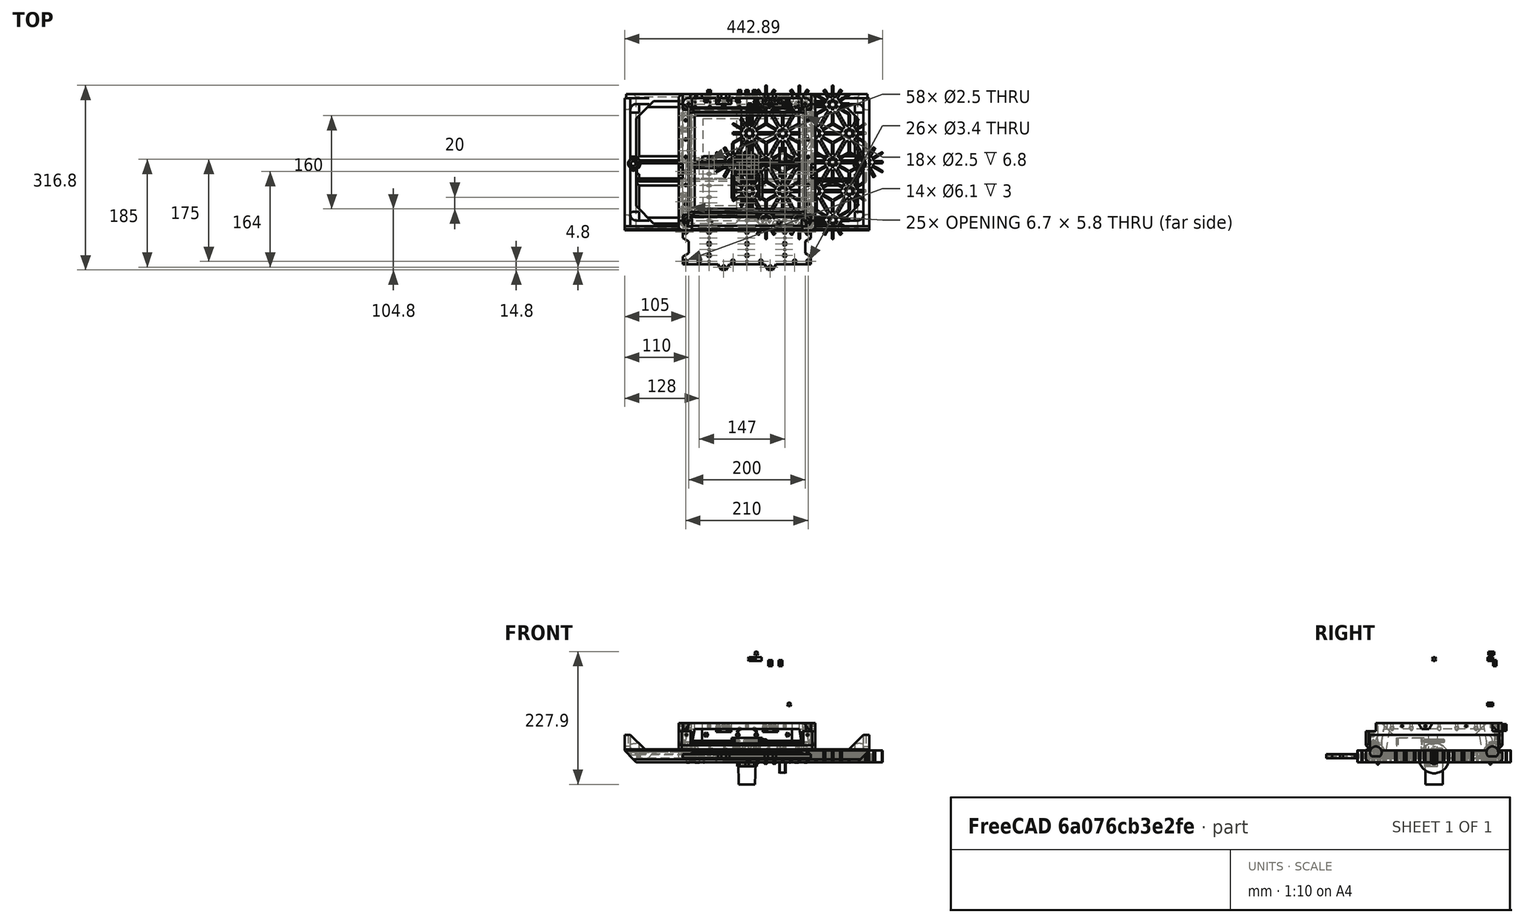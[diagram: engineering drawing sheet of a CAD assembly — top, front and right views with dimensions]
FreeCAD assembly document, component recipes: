
FREECAD ASSEMBLY — COMPONENT RECIPES ("miniXY-Frame")

This assembly document has 23 components, labeled P0..P22 below (a component is one placed body or linked part). 20 of them carry a construction recipe — the FreeCAD feature program that regenerates the part from scratch, quoted from this document or its linked companion documents; the rest are supplied as boundary geometry only. No exploded tour is included for this assembly.
NOTE — this tour is split across 3 documents so each fits a 32k-token context. This is document 1: the component sections continue in the remaining 2 documents, each repeating the header above.
COMPONENT P0 — recipe-attached ("RightPanelKumikoSakura", modeled in this document).
Construction recipe (the document's own serialized feature program — sketch geometry with constraints, then the solid features built on it; lengths are millimeters unless a unit is written):

FEATURE [Sketcher::SketchObject] Sketch076
  FullyConstrained = true
  MapMode = 5
  Support = -> [XY_Plane035]
  expr: Constraints[9] = <<Variables>>.GantorySpacing - 10
  sketch-geometry (4):
    g0: LineSegment StartX=15 StartY=95 StartZ=0 EndX=165 EndY=95 EndZ=0
    g1: LineSegment StartX=165 StartY=95 StartZ=0 EndX=165 EndY=-95 EndZ=0
    g2: LineSegment StartX=165 StartY=-95 StartZ=0 EndX=15 EndY=-95 EndZ=0
    g3: LineSegment StartX=15 StartY=-95 StartZ=0 EndX=15 EndY=95 EndZ=0
  constraints (10):
    c: Coincident(g0,g1)
    c: Coincident(g1,g2)
    c: Coincident(g2,g3)
    c: Coincident(g3,g0)
    c: Symmetric(g0,g2,g-1)
    c: Symmetric(g0,g1,g-1)
    c: DistanceX(g0) = 15
    c: Horizontal(g0)
    c: DistanceX(g0) = 165
    c: DistanceY(g1,g1) = 190
FEATURE [PartDesign::Pad] Pad021
  Direction = (0,0,1)
  Length = 7
  Length2 = 10
  Profile = -> Sketch076
  ReferenceAxis = -> Sketch076 [N_Axis]
  Reversed = true
  Type = 0
  expr: Length = <<Variables>>.WallThickness
FEATURE [PartDesign::Boolean] Boolean001
  BaseFeature = -> Pad021
  Group = -> [Clone045]
  Type = 2
FEATURE [PartDesign::Body] Body019  label="RightPanelKumikoSakura"
  Group = -> [Sketch076,Pad021,Boolean001]
  Origin = -> Origin035
  Tip = -> Boolean001
COMPONENT P1 — recipe-attached ("TopPanelInsertedNuts", modeled in this document).
Construction recipe (the document's own serialized feature program — sketch geometry with constraints, then the solid features built on it; lengths are millimeters unless a unit is written):

FEATURE [PartDesign::AdditiveBox] Box
  AttacherType = Attacher::AttachEngine3D
  AttachmentOffset = pos=(-110,-100,-1) rot=(0,0,1;0rad)
  Height = 1
  Length = 220
  MapMode = 5
  Placement = pos=(-110,-100,-1) rot=(0,0,1;0rad)
  Support = -> [XY_Plane037]
  Width = 200
  expr: .AttachmentOffset.Base.x = -(<<Variables>>.GantorySpacing + 20) / 2
  expr: .AttachmentOffset.Base.y = -<<Variables>>.GantorySpacing / 2
  expr: Length = <<Variables>>.GantorySpacing + 20
  expr: Width = <<Variables>>.GantorySpacing
FEATURE [PartDesign::AdditivePrism] Prism
  AttacherType = Attacher::AttachEngine3D
  AttachmentOffset = pos=(100,80,-1) rot=(0,0,1;0rad)
  BaseFeature = -> Box
  Circumradius = 3.35
  FirstAngle = 0
  Height = 4
  MapMode = 5
  Placement = pos=(100,80,-1) rot=(0,0,1;0rad)
  Polygon = 6
  SecondAngle = 0
  Support = -> [XY_Plane037]
  expr: .AttachmentOffset.Base.x = <<Variables>>.GantorySpacing / 2
  expr: .AttachmentOffset.Base.y = trunc((<<Variables>>.GantorySpacing - 20) / 20 / 2) * 20
FEATURE [PartDesign::AdditivePrism] Prism020
  AttacherType = Attacher::AttachEngine3D
  AttachmentOffset = pos=(-100,80,-1) rot=(0,0,1;0rad)
  BaseFeature = -> Prism
  Circumradius = 3.35
  FirstAngle = 0
  Height = 4
  MapMode = 5
  Placement = pos=(-100,80,-1) rot=(0,0,1;0rad)
  Polygon = 6
  SecondAngle = 0
  Support = -> [XY_Plane037]
  expr: .AttachmentOffset.Base.x = -<<Variables>>.GantorySpacing / 2
  expr: .AttachmentOffset.Base.y = trunc((<<Variables>>.GantorySpacing - 20) / 20 / 2) * 20
FEATURE [PartDesign::LinearPattern] LinearPattern
  BaseFeature = -> Prism020
  Direction = -> Y_Axis037
  Length = 160
  Occurrences = 9
  Originals = -> [Prism,Prism020]
  Placement = pos=(-100,80,-1) rot=(0,0,1;0rad)
  Reversed = true
  expr: Length = trunc((<<Variables>>.GantorySpacing - 1) / 20 - 1) * 20
  expr: Occurrences = trunc((<<Variables>>.GantorySpacing - 1) / 20)
FEATURE [PartDesign::Body] Body021  label="TopPanelInsertedNuts"
  Group = -> [Box,Prism,Prism020,LinearPattern]
  Origin = -> Origin037
  Tip = -> LinearPattern
COMPONENT P2 — geometry summary ("LeftPanel"; no construction recipe available for this part):
  bounding box: 234.0 x 210.0 x 47.0 mm
  tessellated surface: 684 triangles
  volume: 478904856520590275852955231166615715246145621785509215956463249338484086506495282965888048924409776630849818438009607219283139737538738958728098922627072 mm^3 (20735582076420394415876391785394331561649271033872828819312797242641532115541347280385334868308949145231766654478375564196134222345893274777731203072% of its bounding box)
COMPONENT P3 — geometry summary ("LeftPullyMount"; no construction recipe available for this part):
  bounding box: 24.0 x 23.0 x 23.0 mm
  tessellated surface: 248 triangles
  volume: 299315535325368910778677430749424573239660087407870710314527759839463589562716364963451420763389337175224325103538955539851616635702864912651435768807424 mm^3 (2360107169195797858979530859132323100612416590760435877303002830261131174156394113953131164970302059916367937818172666815640445996735709350483468484608% of its bounding box)
COMPONENT P4 — recipe-attached ("PullyIdler", modeled in this document).
Construction recipe (the document's own serialized feature program — sketch geometry with constraints, then the solid features built on it; lengths are millimeters unless a unit is written):

FEATURE [Sketcher::SketchObject] Sketch004
  FullyConstrained = true
  MapMode = 5
  Placement = pos=(0,0,0) rot=(1,0,0;1.5708rad)
  Support = -> [XZ_Plane003]
  expr: Constraints[19] = <<Variables>>.PullyDiameterIdler / 2
  sketch-geometry (8):
    g0: LineSegment StartX=2.5 StartY=4.25 StartZ=0 EndX=2.5 EndY=-4.25 EndZ=0
    g1: LineSegment StartX=2.5 StartY=-4.25 StartZ=0 EndX=9 EndY=-4.25 EndZ=0
    g2: LineSegment StartX=9 StartY=-4.25 StartZ=0 EndX=9 EndY=-3.25 EndZ=0
    g3: LineSegment StartX=9 StartY=-3.25 StartZ=0 EndX=6.365 EndY=-3.25 EndZ=0
    g4: LineSegment StartX=6.365 StartY=-3.25 StartZ=0 EndX=6.365 EndY=3.25 EndZ=0
    g5: LineSegment StartX=6.365 StartY=3.25 StartZ=0 EndX=9 EndY=3.25 EndZ=0
    g6: LineSegment StartX=9 StartY=3.25 StartZ=0 EndX=9 EndY=4.25 EndZ=0
    g7: LineSegment StartX=9 StartY=4.25 StartZ=0 EndX=2.5 EndY=4.25 EndZ=0
  constraints (22):
    c: Coincident(g0,g1)
    c: Horizontal(g1)
    c: Coincident(g1,g2)
    c: Vertical(g2)
    c: Coincident(g2,g3)
    c: Horizontal(g3)
    c: Coincident(g3,g4)
    c: Coincident(g4,g5)
    c: Horizontal(g5)
    c: Coincident(g5,g6)
    c: Vertical(g6)
    c: Coincident(g6,g7)
    c: Coincident(g7,g0)
    c: Horizontal(g7)
    c: Symmetric(g0,g0,g-1)
    c: Symmetric(g4,g3,g-1)
    c: DistanceY(g6,g6) = 1
    c: DistanceY(g4,g4) = 6.5
    c: DistanceX(g-1,g0) = 2.5
    c: DistanceX(g-1,g4) = 6.365
    c: DistanceX(g-1,g6) = 9
    c: Vertical(g2,g5)
FEATURE [PartDesign::Revolution] Revolution
  Angle = 360
  Axis = (0,-2e-16,1)
  Base = (0,0,0)
  Placement = pos=(0,0,0) rot=(1,0,0;1.5708rad)
  Profile = -> Sketch004
  ReferenceAxis = -> Sketch004 [V_Axis]
FEATURE [PartDesign::Body] Body  label="IdlerBody"
  Group = -> [Sketch004,Revolution]
  Origin = -> Origin003
  Tip = -> Revolution
COMPONENT P5 — recipe-attached ("CarriageLeft", modeled in this document).
Construction recipe (the document's own serialized feature program — sketch geometry with constraints, then the solid features built on it; lengths are millimeters unless a unit is written):

FEATURE [Sketcher::SketchObject] Sketch
  FullyConstrained = true
  MapMode = 5
  Support = -> [XY_Plane006]
  sketch-geometry (19):
    g0: LineSegment StartX=-7.5 StartY=16 StartZ=0 EndX=7.5 EndY=16 EndZ=0
    g1: LineSegment StartX=7.5 StartY=-16 StartZ=0 EndX=-7.5 EndY=-16 EndZ=0
    g2: LineSegment StartX=-10 StartY=-13.5 StartZ=0 EndX=-10 EndY=13.5 EndZ=0
    g3: LineSegment StartX=20.7665 StartY=5 StartZ=0 EndX=48 EndY=5 EndZ=0
    g4: LineSegment StartX=50 StartY=3 StartZ=0 EndX=50 EndY=-3 EndZ=0
    g5: LineSegment StartX=48 StartY=-5 StartZ=0 EndX=20.7665 EndY=-5 EndZ=0
    g6: ArcOfCircle CenterX=20.7665 CenterY=-16 CenterZ=0 NormalX=0 NormalY=0 NormalZ=1 AngleXU=0 Radius=11 StartAngle=1.5708 EndAngle=2.95533
    g7: ArcOfCircle CenterX=20.7665 CenterY=16 CenterZ=0 NormalX=0 NormalY=0 NormalZ=1 AngleXU=0 Radius=11 StartAngle=3.32785 EndAngle=4.71239
    g8: ArcOfCircle CenterX=-7.5 CenterY=13.5 CenterZ=0 NormalX=0 NormalY=0 NormalZ=1 AngleXU=0 Radius=2.5 StartAngle=1.5708 EndAngle=3.14159
    g9: GeomPoint X=-10 Y=16 Z=0
    g10: ArcOfCircle CenterX=-7.5 CenterY=-13.5 CenterZ=0 NormalX=0 NormalY=0 NormalZ=1 AngleXU=0 Radius=2.5 StartAngle=3.14159 EndAngle=4.71239
    g11: GeomPoint X=-10 Y=-16 Z=0
    g12: ArcOfCircle CenterX=7.5 CenterY=-13.5 CenterZ=0 NormalX=0 NormalY=0 NormalZ=1 AngleXU=0 Radius=2.5 StartAngle=4.71239 EndAngle=6.09693
    g13: ArcOfCircle CenterX=7.5 CenterY=13.5 CenterZ=0 NormalX=0 NormalY=0 NormalZ=1 AngleXU=0 Radius=2.5 StartAngle=0.18626 EndAngle=1.5708
    g14: GeomPoint X=10 Y=16 Z=0
    g15: ArcOfCircle CenterX=48 CenterY=3 CenterZ=0 NormalX=0 NormalY=0 NormalZ=1 AngleXU=0 Radius=2 StartAngle=-9e-16 EndAngle=1.5708
    g16: GeomPoint X=50 Y=5 Z=0
    g17: ArcOfCircle CenterX=48 CenterY=-3 CenterZ=0 NormalX=0 NormalY=0 NormalZ=1 AngleXU=0 Radius=2 StartAngle=4.71239 EndAngle=6.28319
    g18: GeomPoint X=50 Y=-5 Z=0
  constraints (40):
    c: Horizontal(g3)
    c: Symmetric(g9,g11,g-1)
    c: Symmetric(g16,g18,g-1)
    c: DistanceY(g11,g9) = 32
    c: Symmetric(g9,g14,g-2)
    c: DistanceY(g18,g16) = 10
    c: DistanceX(g-1,g16) = 50
    c: Symmetric(g7,g6,g-1)
    c: PointOnObject(g9,g0)
    c: PointOnObject(g9,g2)
    c: Tangent(g0,g8) = 1.5708
    c: Tangent(g2,g8) = 1.5708
    c: PointOnObject(g11,g2)
    c: PointOnObject(g11,g1)
    c: Tangent(g2,g10) = 1.5708
    c: Tangent(g1,g10) = 1.5708
    c: Tangent(g1,g12) = 1.5708
    c: PointOnObject(g14,g0)
    c: Tangent(g0,g13) = 1.5708
    c: Equal(g8,g10)
    c: Equal(g8,g12)
    c: Radius(g8) = 2.5
    c: DistanceX(g9,g14) = 20
    c: Tangent(g13,g7) = 1.5708
    c: Tangent(g12,g6) = 1.5708
    c: PointOnObject(g7,g0)
    c: Symmetric(g8,g13,g-2)
    c: Symmetric(g12,g13,g-1)
    c: Tangent(g7,g3) = -1.5708
    c: Tangent(g6,g5) = -1.5708
    c: PointOnObject(g16,g3)
    c: PointOnObject(g16,g4)
    c: Tangent(g3,g15) = 1.5708
    c: Tangent(g4,g15) = 1.5708
    c: PointOnObject(g18,g5)
    c: PointOnObject(g18,g4)
    c: Tangent(g5,g17) = 1.5708
    c: Tangent(g4,g17) = 1.5708
    c: Equal(g15,g17)
    c: Radius(g15) = 2
FEATURE [PartDesign::Pad] Pad
  Direction = (0,0,1)
  Length = 7
  Length2 = 10
  Profile = -> Sketch
  ReferenceAxis = -> Sketch [N_Axis]
  Type = 0
FEATURE [Sketcher::SketchObject] Sketch005
  AttachmentOffset = pos=(0,0,10) rot=(0,0,1;0rad)
  FullyConstrained = true
  MapMode = 5
  Placement = pos=(0,0,10) rot=(0,0,1;0rad)
  Support = -> [XY_Plane006]
  sketch-geometry (4):
    g0: Circle CenterX=-7.5 CenterY=5 CenterZ=0 NormalX=0 NormalY=0 NormalZ=1 AngleXU=0 Radius=1.5
    g1: Circle CenterX=-7.5 CenterY=-5 CenterZ=0 NormalX=0 NormalY=0 NormalZ=1 AngleXU=0 Radius=1.5
    g2: Circle CenterX=7.5 CenterY=-5 CenterZ=0 NormalX=0 NormalY=0 NormalZ=1 AngleXU=0 Radius=1.5
    g3: Circle CenterX=7.5 CenterY=5 CenterZ=0 NormalX=0 NormalY=0 NormalZ=1 AngleXU=0 Radius=1.5
  constraints (9):
    c: Symmetric(g0,g1,g-1)
    c: Symmetric(g3,g2,g-1)
    c: Symmetric(g0,g3,g-2)
    c: DistanceX(g0,g3) = 15
    c: DistanceY(g1,g0) = 10
    c: Equal(g0,g1)
    c: Equal(g0,g2)
    c: Equal(g0,g3)
    c: Diameter(g0) = 3
FEATURE [Sketcher::SketchObject] Sketch006
  FullyConstrained = true
  MapMode = 5
  Support = -> [XY_Plane006]
  sketch-geometry (2):
    g0: Circle CenterX=0 CenterY=0 CenterZ=0 NormalX=0 NormalY=0 NormalZ=1 AngleXU=0 Radius=1.5
    g1: Circle CenterX=12.73 CenterY=0 CenterZ=0 NormalX=0 NormalY=0 NormalZ=1 AngleXU=0 Radius=1.5
  constraints (5):
    c: Coincident(g0,g-1)
    c: PointOnObject(g1,g-1)
    c: Equal(g0,g1)
    c: Diameter(g0) = 3
    c: DistanceX(g0,g1) = 12.73
FEATURE [PartDesign::Chamfer] Chamfer
  Angle = 45
  Base = -> Pad [Face16]
  BaseFeature = -> Pad
  ChamferType = 0
  FlipDirection = false
  Size = 1
  Size2 = 1
  SupportTransform = false
  UseAllEdges = false
FEATURE [Sketcher::SketchObject] Sketch007
  FullyConstrained = true
  MapMode = 5
  Support = -> [XY_Plane006]
  sketch-geometry (2):
    g0: Circle CenterX=20 CenterY=0 CenterZ=0 NormalX=0 NormalY=0 NormalZ=1 AngleXU=0 Radius=1.5
    g1: Circle CenterX=40 CenterY=0 CenterZ=0 NormalX=0 NormalY=0 NormalZ=1 AngleXU=0 Radius=1.5
  constraints (6):
    c: PointOnObject(g0,g-1)
    c: PointOnObject(g1,g-1)
    c: DistanceX(g-1,g0) = 20
    c: DistanceX(g0,g1) = 20
    c: Equal(g0,g1)
    c: Diameter(g0) = 3
FEATURE [Sketcher::SketchObject] Sketch008
  AttachmentOffset = pos=(0,0,16.5) rot=(0,0,1;0rad)
  FullyConstrained = true
  MapMode = 5
  Placement = pos=(0,0,16.5) rot=(0,0,1;0rad)
  Support = -> [XY_Plane006]
  sketch-geometry (6):
    g0: LineSegment StartX=9.5 StartY=5 StartZ=0 EndX=26 EndY=5 EndZ=0
    g1: LineSegment StartX=24 StartY=3 StartZ=0 EndX=24 EndY=-3 EndZ=0
    g2: LineSegment StartX=26 StartY=-5 StartZ=0 EndX=9.5 EndY=-5 EndZ=0
    g3: LineSegment StartX=9.5 StartY=-5 StartZ=0 EndX=9.5 EndY=5 EndZ=0
    g4: ArcOfCircle CenterX=26 CenterY=3 CenterZ=0 NormalX=0 NormalY=0 NormalZ=1 AngleXU=0 Radius=2 StartAngle=1.5708 EndAngle=3.14159
    g5: ArcOfCircle CenterX=26 CenterY=-3 CenterZ=0 NormalX=0 NormalY=0 NormalZ=1 AngleXU=0 Radius=2 StartAngle=3.14159 EndAngle=4.71239
  constraints (14):
    c: Horizontal(g0)
    c: Coincident(g0,g3)
    c: Symmetric(g2,g0,g-1)
    c: Coincident(g3,g2)
    c: Tangent(g4,g1) = -1.5708
    c: Tangent(g4,g0) = 1.5708
    c: Tangent(g5,g1) = -1.5708
    c: Tangent(g5,g2) = 1.5708
    c: Symmetric(g4,g5,g-1)
    c: Equal(g4,g5)
    c: Radius(g4) = 2
    c: DistanceY(g3,g3) = 10
    c: DistanceX(g0,g1) = 14.5
    c: DistanceX(g-1,g0) = 9.5
FEATURE [Sketcher::SketchObject] Sketch009
  FullyConstrained = true
  MapMode = 5
  Support = -> [XY_Plane006]
  sketch-geometry (36):
    g0: LineSegment StartX=11.5 StartY=5 StartZ=0 EndX=30 EndY=5 EndZ=0
    g1: LineSegment StartX=32 StartY=3 StartZ=0 EndX=32 EndY=-3 EndZ=0
    g2: LineSegment StartX=30 StartY=-5 StartZ=0 EndX=11.5 EndY=-5 EndZ=0
    g3: LineSegment StartX=9.5 StartY=-3 StartZ=0 EndX=9.5 EndY=3 EndZ=0
    g4: LineSegment StartX=-3 StartY=16 StartZ=0 EndX=3 EndY=16 EndZ=0
    g5: LineSegment StartX=5 StartY=14 StartZ=0 EndX=5 EndY=12 EndZ=0
    g6: LineSegment StartX=3 StartY=10 StartZ=0 EndX=-3 EndY=10 EndZ=0
    g7: LineSegment StartX=-5 StartY=12 StartZ=0 EndX=-5 EndY=14 EndZ=0
    g8: LineSegment StartX=-3 StartY=-10 StartZ=0 EndX=3 EndY=-10 EndZ=0
    g9: LineSegment StartX=5 StartY=-12 StartZ=0 EndX=5 EndY=-14 EndZ=0
    g10: LineSegment StartX=3 StartY=-16 StartZ=0 EndX=-3 EndY=-16 EndZ=0
    g11: LineSegment StartX=-5 StartY=-14 StartZ=0 EndX=-5 EndY=-12 EndZ=0
    g12: ArcOfCircle CenterX=-3 CenterY=14 CenterZ=0 NormalX=0 NormalY=0 NormalZ=1 AngleXU=0 Radius=2 StartAngle=1.5708 EndAngle=3.14159
    g13: GeomPoint X=-5 Y=16 Z=0
    g14: ArcOfCircle CenterX=-3 CenterY=12 CenterZ=0 NormalX=0 NormalY=0 NormalZ=1 AngleXU=0 Radius=2 StartAngle=3.14159 EndAngle=4.71239
    g15: GeomPoint X=-5 Y=10 Z=0
    g16: ArcOfCircle CenterX=3 CenterY=12 CenterZ=0 NormalX=0 NormalY=0 NormalZ=1 AngleXU=0 Radius=2 StartAngle=4.71239 EndAngle=6.28319
    g17: GeomPoint X=5 Y=10 Z=0
    g18: ArcOfCircle CenterX=3 CenterY=14 CenterZ=0 NormalX=0 NormalY=0 NormalZ=1 AngleXU=0 Radius=2 StartAngle=1e-16 EndAngle=1.5708
    g19: GeomPoint X=5 Y=16 Z=0
    g20: ArcOfCircle CenterX=-3 CenterY=-12 CenterZ=0 NormalX=0 NormalY=0 NormalZ=1 AngleXU=0 Radius=2 StartAngle=1.5708 EndAngle=3.14159
    g21: GeomPoint X=-5 Y=-10 Z=0
    g22: ArcOfCircle CenterX=-3 CenterY=-14 CenterZ=0 NormalX=0 NormalY=0 NormalZ=1 AngleXU=0 Radius=2 StartAngle=3.14159 EndAngle=4.71239
    g23: GeomPoint X=-5 Y=-16 Z=0
    g24: ArcOfCircle CenterX=3 CenterY=-14 CenterZ=0 NormalX=0 NormalY=0 NormalZ=1 AngleXU=0 Radius=2 StartAngle=4.71239 EndAngle=6.28319
    g25: GeomPoint X=5 Y=-16 Z=0
    g26: ArcOfCircle CenterX=3 CenterY=-12 CenterZ=0 NormalX=0 NormalY=0 NormalZ=1 AngleXU=0 Radius=2 StartAngle=0 EndAngle=1.5708
    g27: GeomPoint X=5 Y=-10 Z=0
    g28: ArcOfCircle CenterX=11.5 CenterY=3 CenterZ=0 NormalX=0 NormalY=0 NormalZ=1 AngleXU=0 Radius=2 StartAngle=1.5708 EndAngle=3.14159
    g29: GeomPoint X=9.5 Y=5 Z=0
    g30: ArcOfCircle CenterX=11.5 CenterY=-3 CenterZ=0 NormalX=0 NormalY=0 NormalZ=1 AngleXU=0 Radius=2 StartAngle=3.14159 EndAngle=4.71239
    g31: GeomPoint X=9.5 Y=-5 Z=0
    g32: ArcOfCircle CenterX=30 CenterY=-3 CenterZ=0 NormalX=0 NormalY=0 NormalZ=1 AngleXU=0 Radius=2 StartAngle=4.71239 EndAngle=6.28319
    g33: GeomPoint X=32 Y=-5 Z=0
    g34: ArcOfCircle CenterX=30 CenterY=3 CenterZ=0 NormalX=0 NormalY=0 NormalZ=1 AngleXU=0 Radius=2 StartAngle=3e-16 EndAngle=1.5708
    g35: GeomPoint X=32 Y=5 Z=0
  constraints (76):
    c: Horizontal(g0)
    c: Symmetric(g29,g31,g-1)
    c: Symmetric(g35,g33,g-1)
    c: DistanceY(g31,g29) = 10
    c: DistanceX(g29,g35) = 22.5
    c: Vertical(g7)
    c: Symmetric(g13,g19,g-2)
    c: Symmetric(g15,g17,g-2)
    c: Symmetric(g21,g15,g-1)
    c: Symmetric(g13,g23,g-1)
    c: Symmetric(g17,g27,g-1)
    c: Symmetric(g19,g25,g-1)
    c: DistanceY(g23,g13) = 32
    c: DistanceX(g13,g19) = 10
    c: DistanceY(g15,g13) = 6
    c: DistanceX(g-1,g35) = 32
    c: PointOnObject(g13,g4)
    c: PointOnObject(g13,g7)
    c: Tangent(g4,g12) = 1.5708
    c: Tangent(g7,g12) = 1.5708
    c: PointOnObject(g15,g7)
    c: PointOnObject(g15,g6)
    c: Tangent(g7,g14) = 1.5708
    c: Tangent(g6,g14) = 1.5708
    c: PointOnObject(g17,g6)
    c: PointOnObject(g17,g5)
    c: Tangent(g6,g16) = 1.5708
    c: Tangent(g5,g16) = 1.5708
    c: PointOnObject(g19,g5)
    c: PointOnObject(g19,g4)
    c: Tangent(g5,g18) = 1.5708
    c: Tangent(g4,g18) = 1.5708
    c: PointOnObject(g21,g8)
    c: PointOnObject(g21,g11)
    c: Tangent(g8,g20) = 1.5708
    c: Tangent(g11,g20) = 1.5708
    c: PointOnObject(g23,g11)
    c: PointOnObject(g23,g10)
    c: Tangent(g11,g22) = 1.5708
    c: Tangent(g10,g22) = 1.5708
    c: PointOnObject(g25,g10)
    c: PointOnObject(g25,g9)
    c: Tangent(g10,g24) = 1.5708
    c: Tangent(g9,g24) = 1.5708
    c: PointOnObject(g27,g9)
    c: PointOnObject(g27,g8)
    c: Tangent(g9,g26) = 1.5708
    c: Tangent(g8,g26) = 1.5708
    c: PointOnObject(g29,g0)
    c: PointOnObject(g29,g3)
    c: Tangent(g0,g28) = 1.5708
    c: Tangent(g3,g28) = 1.5708
    c: PointOnObject(g31,g3)
    c: PointOnObject(g31,g2)
    c: Tangent(g3,g30) = 1.5708
    c: Tangent(g2,g30) = 1.5708
    c: PointOnObject(g33,g2)
    c: PointOnObject(g33,g1)
    c: Tangent(g2,g32) = 1.5708
    c: Tangent(g1,g32) = 1.5708
    c: PointOnObject(g35,g1)
    c: PointOnObject(g35,g0)
    c: Tangent(g1,g34) = 1.5708
    c: Tangent(g0,g34) = 1.5708
    c: Equal(g12,g14)
    c: Equal(g12,g16)
    c: Equal(g12,g18)
    c: Equal(g12,g20)
    c: Equal(g12,g22)
    c: Equal(g12,g24)
    c: Equal(g12,g26)
    c: Equal(g12,g28)
    c: Equal(g12,g30)
    c: Equal(g12,g32)
    c: Equal(g12,g34)
    c: Radius(g12) = 2
FEATURE [Sketcher::SketchObject] Sketch010
  FullyConstrained = true
  MapMode = 5
  Support = -> [XY_Plane006]
  sketch-geometry (2):
    g0: Circle CenterX=0 CenterY=13 CenterZ=0 NormalX=0 NormalY=0 NormalZ=1 AngleXU=0 Radius=1.5
    g1: Circle CenterX=0 CenterY=-13 CenterZ=0 NormalX=0 NormalY=0 NormalZ=1 AngleXU=0 Radius=1.5
  constraints (5):
    c: PointOnObject(g0,g-2)
    c: Symmetric(g0,g1,g-1)
    c: DistanceY(g1,g0) = 26
    c: Equal(g0,g1)
    c: Diameter(g0) = 3
FEATURE [Sketcher::SketchObject] Sketch011
  AttachmentOffset = pos=(0,0,27) rot=(0,0,1;0rad)
  FullyConstrained = true
  MapMode = 5
  Placement = pos=(0,0,27) rot=(0,0,1;0rad)
  Support = -> [XY_Plane008]
  sketch-geometry (8):
    g0: LineSegment StartX=-5 StartY=18 StartZ=0 EndX=5 EndY=18 EndZ=0
    g1: LineSegment StartX=5 StartY=-18 StartZ=0 EndX=-5 EndY=-18 EndZ=0
    g2: LineSegment StartX=-5 StartY=-18 StartZ=0 EndX=-5 EndY=18 EndZ=0
    g3: LineSegment StartX=18.5 StartY=4.5 StartZ=0 EndX=34 EndY=4.5 EndZ=0
    g4: LineSegment StartX=34 StartY=4.5 StartZ=0 EndX=34 EndY=-4.5 EndZ=0
    g5: LineSegment StartX=34 StartY=-4.5 StartZ=0 EndX=18.5 EndY=-4.5 EndZ=0
    g6: ArcOfCircle CenterX=18.5 CenterY=-18 CenterZ=0 NormalX=0 NormalY=0 NormalZ=1 AngleXU=0 Radius=13.5 StartAngle=1.5708 EndAngle=3.14159
    g7: ArcOfCircle CenterX=18.5 CenterY=18 CenterZ=0 NormalX=0 NormalY=0 NormalZ=1 AngleXU=0 Radius=13.5 StartAngle=3.14159 EndAngle=4.71239
  constraints (21):
    c: Coincident(g1,g2)
    c: Coincident(g2,g0)
    c: Coincident(g3,g4)
    c: Coincident(g4,g5)
    c: Horizontal(g3)
    c: Symmetric(g0,g1,g-1)
    c: Symmetric(g3,g5,g-1)
    c: Symmetric(g3,g4,g-1)
    c: DistanceY(g2,g2) = 36
    c: DistanceX(g0,g0) = 10
    c: Symmetric(g0,g0,g-2)
    c: DistanceY(g4,g4) = 9
    c: Symmetric(g0,g1,g-1)
    c: DistanceX(g-1,g3) = 34
    c: Coincident(g6,g5)
    c: Coincident(g6,g1)
    c: Coincident(g7,g0)
    c: Coincident(g7,g3)
    c: Symmetric(g7,g6,g-1)
    c: Vertical(g7,g3)
    c: Horizontal(g0,g7)
FEATURE [PartDesign::Pad] Pad003
  Direction = (0,0,1)
  Length = 5
  Length2 = 10
  Profile = -> Sketch011
  ReferenceAxis = -> Sketch011 [N_Axis]
  Type = 0
FEATURE [PartDesign::SubtractiveBox] Box003
  AttacherType = Attacher::AttachEngine3D
  AttachmentOffset = pos=(-3.1,9.9,0) rot=(0,0,1;0rad)
  BaseFeature = -> Pad003
  Height = 28
  Length = 6.2
  MapMode = 5
  Placement = pos=(-3.1,9.9,0) rot=(0,0,1;0rad)
  Support = -> [XY_Plane008]
  Width = 6.2
FEATURE [PartDesign::SubtractiveBox] Box004
  AttacherType = Attacher::AttachEngine3D
  AttachmentOffset = pos=(-3.1,-16.1,0) rot=(0,0,1;0rad)
  BaseFeature = -> Box003
  Height = 28
  Length = 6.2
  MapMode = 5
  Placement = pos=(-3.1,-16.1,0) rot=(0,0,1;0rad)
  Support = -> [XY_Plane008]
  Width = 6.2
FEATURE [PartDesign::SubtractiveBox] Box005
  AttacherType = Attacher::AttachEngine3D
  AttachmentOffset = pos=(23.9,-3.1,0) rot=(0,0,1;0rad)
  BaseFeature = -> Box004
  Height = 28
  Length = 8.2
  MapMode = 5
  Placement = pos=(23.9,-3.1,0) rot=(0,0,1;0rad)
  Support = -> [XY_Plane008]
  Width = 6.2
FEATURE [PartDesign::Fillet] Fillet002
  Base = -> Box005 [Edge41,Edge57,Edge49,Edge39,Edge55,Edge47,Edge45,Edge37,Edge53,Edge59,Edge51,Edge43]
  BaseFeature = -> Box005
  Placement = pos=(23.9,-3.1,0) rot=(0,0,1;0rad)
  Radius = 0.8
  SupportTransform = false
  UseAllEdges = false
FEATURE [PartDesign::Fillet] Fillet003
  Base = -> Fillet002 [Edge56,Edge52,Edge62,Edge50,Edge49,Edge58]
  BaseFeature = -> Fillet002
  Placement = pos=(23.9,-3.1,0) rot=(0,0,1;0rad)
  Radius = 2.5
  SupportTransform = false
  UseAllEdges = false
FEATURE [PartDesign::Chamfer] Chamfer001
  Angle = 45
  Base = -> Fillet003 [Edge4]
  BaseFeature = -> Fillet003
  ChamferType = 0
  FlipDirection = false
  Placement = pos=(23.9,-3.1,0) rot=(0,0,1;0rad)
  Size = 1
  Size2 = 1
  SupportTransform = false
  UseAllEdges = false
FEATURE [PartDesign::Chamfer] Chamfer002
  Angle = 45
  Base = -> Chamfer001 [Edge116]
  BaseFeature = -> Chamfer001
  ChamferType = 0
  FlipDirection = false
  Placement = pos=(23.9,-3.1,0) rot=(0,0,1;0rad)
  Size = 1
  Size2 = 1
  SupportTransform = false
  UseAllEdges = false
FEATURE [Sketcher::SketchObject] Sketch012
  AttachmentOffset = pos=(0,0,32) rot=(0,0,1;0rad)
  FullyConstrained = true
  MapMode = 5
  Placement = pos=(0,0,32) rot=(0,0,1;0rad)
  Support = -> [XY_Plane008]
  expr: Constraints[4] = <<Variables>>.PullyDiameterIdler
  sketch-geometry (2):
    g0: Circle CenterX=0 CenterY=0 CenterZ=0 NormalX=0 NormalY=0 NormalZ=1 AngleXU=0 Radius=1.5
    g1: Circle CenterX=12.73 CenterY=0 CenterZ=0 NormalX=0 NormalY=0 NormalZ=1 AngleXU=0 Radius=1.5
  constraints (5):
    c: Coincident(g0,g-1)
    c: PointOnObject(g1,g-1)
    c: Equal(g0,g1)
    c: Diameter(g0) = 3
    c: DistanceX(g0,g1) = 12.73
FEATURE [PartDesign::Hole] Hole004
  BaseFeature = -> Chamfer002
  CustomThreadClearance = 0
  Depth = 98.3182
  DepthType = 1
  Diameter = 5.5
  DrillForDepth = false
  DrillPoint = 1
  DrillPointAngle = 118
  HoleCutCountersinkAngle = 90
  HoleCutCustomValues = false
  HoleCutDepth = 5.4
  HoleCutDiameter = 10.1
  HoleCutType = 0
  ModelThread = false
  Placement = pos=(23.9,-3.1,0) rot=(0,0,1;0rad)
  Profile = -> Sketch012
  Tapered = false
  TaperedAngle = 90
  ThreadClass = 0
  ThreadDepth = 98.3182
  ThreadDepthType = 0
  ThreadDirection = 0
  ThreadFit = 0
  ThreadSize = 13
  ThreadType = 1
  Threaded = false
  UseCustomThreadClearance = false
FEATURE [Sketcher::SketchObject] Sketch013
  AttachmentOffset = pos=(0,0,32) rot=(0,0,1;0rad)
  FullyConstrained = true
  MapMode = 5
  Placement = pos=(0,0,32) rot=(0,0,1;0rad)
  Support = -> [XY_Plane008]
  sketch-geometry (3):
    g0: Circle CenterX=0 CenterY=13 CenterZ=0 NormalX=0 NormalY=0 NormalZ=1 AngleXU=0 Radius=1.5
    g1: Circle CenterX=0 CenterY=-13 CenterZ=0 NormalX=0 NormalY=0 NormalZ=1 AngleXU=0 Radius=1.5
    g2: Circle CenterX=28 CenterY=0 CenterZ=0 NormalX=0 NormalY=0 NormalZ=1 AngleXU=0 Radius=1.5
  constraints (8):
    c: PointOnObject(g0,g-2)
    c: PointOnObject(g2,g-1)
    c: Symmetric(g0,g1,g-1)
    c: DistanceY(g1,g0) = 26
    c: DistanceX(g-1,g2) = 28
    c: Equal(g0,g1)
    c: Equal(g0,g2)
    c: Diameter(g0) = 3
FEATURE [PartDesign::Hole] Hole005
  BaseFeature = -> Hole004
  CustomThreadClearance = 0
  Depth = 98.3182
  DepthType = 1
  Diameter = 3.4
  DrillForDepth = false
  DrillPoint = 1
  DrillPointAngle = 118
  HoleCutCountersinkAngle = 90
  HoleCutCustomValues = false
  HoleCutDepth = 1.7
  HoleCutDiameter = 6
  HoleCutType = 9
  ModelThread = false
  Placement = pos=(23.9,-3.1,0) rot=(0,0,1;0rad)
  Profile = -> Sketch013
  Tapered = false
  TaperedAngle = 90
  ThreadClass = 0
  ThreadDepth = 98.3182
  ThreadDepthType = 0
  ThreadDirection = 0
  ThreadFit = 0
  ThreadSize = 9
  ThreadType = 1
  Threaded = false
  UseCustomThreadClearance = false
FEATURE [Sketcher::SketchObject] Sketch078
  FullyConstrained = true
  MapMode = 5
  Support = -> [XY_Plane006]
  sketch-geometry (24):
    g0: LineSegment StartX=-3 StartY=16 StartZ=0 EndX=3 EndY=16 EndZ=0
    g1: LineSegment StartX=5 StartY=14 StartZ=0 EndX=5 EndY=12 EndZ=0
    g2: LineSegment StartX=3 StartY=10 StartZ=0 EndX=-3 EndY=10 EndZ=0
    g3: LineSegment StartX=-5 StartY=12 StartZ=0 EndX=-5 EndY=14 EndZ=0
    g4: LineSegment StartX=-3 StartY=-10 StartZ=0 EndX=3 EndY=-10 EndZ=0
    g5: LineSegment StartX=5 StartY=-12 StartZ=0 EndX=5 EndY=-14 EndZ=0
    g6: LineSegment StartX=3 StartY=-16 StartZ=0 EndX=-3 EndY=-16 EndZ=0
    g7: LineSegment StartX=-5 StartY=-14 StartZ=0 EndX=-5 EndY=-12 EndZ=0
    g8: ArcOfCircle CenterX=-3 CenterY=14 CenterZ=0 NormalX=0 NormalY=0 NormalZ=1 AngleXU=0 Radius=2 StartAngle=1.5708 EndAngle=3.14159
    g9: GeomPoint X=-5 Y=16 Z=0
    g10: ArcOfCircle CenterX=-3 CenterY=12 CenterZ=0 NormalX=0 NormalY=0 NormalZ=1 AngleXU=0 Radius=2 StartAngle=3.14159 EndAngle=4.71239
    g11: GeomPoint X=-5 Y=10 Z=0
    g12: ArcOfCircle CenterX=3 CenterY=12 CenterZ=0 NormalX=0 NormalY=0 NormalZ=1 AngleXU=0 Radius=2 StartAngle=4.71239 EndAngle=6.28319
    g13: GeomPoint X=5 Y=10 Z=0
    g14: ArcOfCircle CenterX=3 CenterY=14 CenterZ=0 NormalX=0 NormalY=0 NormalZ=1 AngleXU=0 Radius=2 StartAngle=0 EndAngle=1.5708
    g15: GeomPoint X=5 Y=16 Z=0
    g16: ArcOfCircle CenterX=-3 CenterY=-12 CenterZ=0 NormalX=0 NormalY=0 NormalZ=1 AngleXU=0 Radius=2 StartAngle=1.5708 EndAngle=3.14159
    g17: GeomPoint X=-5 Y=-10 Z=0
    g18: ArcOfCircle CenterX=-3 CenterY=-14 CenterZ=0 NormalX=0 NormalY=0 NormalZ=1 AngleXU=0 Radius=2 StartAngle=3.14159 EndAngle=4.71239
    g19: GeomPoint X=-5 Y=-16 Z=0
    g20: ArcOfCircle CenterX=3 CenterY=-14 CenterZ=0 NormalX=0 NormalY=0 NormalZ=1 AngleXU=0 Radius=2 StartAngle=4.71239 EndAngle=6.28319
    g21: GeomPoint X=5 Y=-16 Z=0
    g22: ArcOfCircle CenterX=3 CenterY=-12 CenterZ=0 NormalX=0 NormalY=0 NormalZ=1 AngleXU=0 Radius=2 StartAngle=0 EndAngle=1.5708
    g23: GeomPoint X=5 Y=-10 Z=0
  constraints (50):
    c: Vertical(g3)
    c: Symmetric(g9,g15,g-2)
    c: Symmetric(g11,g13,g-2)
    c: Symmetric(g17,g11,g-1)
    c: Symmetric(g9,g19,g-1)
    c: Symmetric(g13,g23,g-1)
    c: Symmetric(g15,g21,g-1)
    c: DistanceY(g19,g9) = 32
    c: DistanceX(g9,g15) = 10
    c: DistanceY(g11,g9) = 6
    c: PointOnObject(g9,g0)
    c: PointOnObject(g9,g3)
    c: Tangent(g0,g8) = 1.5708
    c: Tangent(g3,g8) = 1.5708
    c: PointOnObject(g11,g3)
    c: PointOnObject(g11,g2)
    c: Tangent(g3,g10) = 1.5708
    c: Tangent(g2,g10) = 1.5708
    c: PointOnObject(g13,g2)
    c: PointOnObject(g13,g1)
    c: Tangent(g2,g12) = 1.5708
    c: Tangent(g1,g12) = 1.5708
    c: PointOnObject(g15,g1)
    c: PointOnObject(g15,g0)
    c: Tangent(g1,g14) = 1.5708
    c: Tangent(g0,g14) = 1.5708
    c: PointOnObject(g17,g4)
    c: PointOnObject(g17,g7)
    c: Tangent(g4,g16) = 1.5708
    c: Tangent(g7,g16) = 1.5708
    c: PointOnObject(g19,g7)
    c: PointOnObject(g19,g6)
    c: Tangent(g7,g18) = 1.5708
    c: Tangent(g6,g18) = 1.5708
    c: PointOnObject(g21,g6)
    c: PointOnObject(g21,g5)
    c: Tangent(g6,g20) = 1.5708
    c: Tangent(g5,g20) = 1.5708
    c: PointOnObject(g23,g5)
    c: PointOnObject(g23,g4)
    c: Tangent(g5,g22) = 1.5708
    c: Tangent(g4,g22) = 1.5708
    c: Equal(g8,g10)
    c: Equal(g8,g12)
    c: Equal(g8,g14)
    c: Equal(g8,g16)
    c: Equal(g8,g18)
    c: Equal(g8,g20)
    c: Equal(g8,g22)
    c: Radius(g8) = 2
FEATURE [Sketcher::SketchObject] Sketch079
  FullyConstrained = true
  MapMode = 5
  Support = -> [XY_Plane006]
  sketch-geometry (12):
    g0: LineSegment StartX=11.5 StartY=5 StartZ=0 EndX=14 EndY=5 EndZ=0
    g1: LineSegment StartX=16 StartY=3 StartZ=0 EndX=16 EndY=-3 EndZ=0
    g2: LineSegment StartX=14 StartY=-5 StartZ=0 EndX=11.5 EndY=-5 EndZ=0
    g3: LineSegment StartX=9.5 StartY=-3 StartZ=0 EndX=9.5 EndY=3 EndZ=0
    g4: ArcOfCircle CenterX=11.5 CenterY=3 CenterZ=0 NormalX=0 NormalY=0 NormalZ=1 AngleXU=0 Radius=2 StartAngle=1.5708 EndAngle=3.14159
    g5: GeomPoint X=9.5 Y=5 Z=0
    g6: ArcOfCircle CenterX=11.5 CenterY=-3 CenterZ=0 NormalX=0 NormalY=0 NormalZ=1 AngleXU=0 Radius=2 StartAngle=3.14159 EndAngle=4.71239
    g7: GeomPoint X=9.5 Y=-5 Z=0
    g8: ArcOfCircle CenterX=14 CenterY=-3 CenterZ=0 NormalX=0 NormalY=0 NormalZ=1 AngleXU=0 Radius=2 StartAngle=4.71239 EndAngle=6.28319
    g9: GeomPoint X=16 Y=-5 Z=0
    g10: ArcOfCircle CenterX=14 CenterY=3 CenterZ=0 NormalX=0 NormalY=0 NormalZ=1 AngleXU=0 Radius=2 StartAngle=0 EndAngle=1.5708
    g11: GeomPoint X=16 Y=5 Z=0
  constraints (26):
    c: Horizontal(g0)
    c: Symmetric(g5,g7,g-1)
    c: Symmetric(g11,g9,g-1)
    c: DistanceY(g7,g5) = 10
    c: DistanceX(g5,g11) = 6.5
    c: PointOnObject(g5,g0)
    c: PointOnObject(g5,g3)
    c: Tangent(g0,g4) = 1.5708
    c: Tangent(g3,g4) = 1.5708
    c: PointOnObject(g7,g3)
    c: PointOnObject(g7,g2)
    c: Tangent(g3,g6) = 1.5708
    c: Tangent(g2,g6) = 1.5708
    c: PointOnObject(g9,g2)
    c: PointOnObject(g9,g1)
    c: Tangent(g2,g8) = 1.5708
    c: Tangent(g1,g8) = 1.5708
    c: PointOnObject(g11,g1)
    c: PointOnObject(g11,g0)
    c: Tangent(g1,g10) = 1.5708
    c: Tangent(g0,g10) = 1.5708
    c: DistanceX(g-1,g5) = 9.5
    c: Equal(g4,g10)
    c: Equal(g4,g6)
    c: Equal(g4,g8)
    c: Radius(g4) = 2
FEATURE [PartDesign::Pad] Pad023
  BaseFeature = -> Chamfer
  Direction = (0,0,1)
  Length = 16.5
  Length2 = 10
  Profile = -> Sketch079
  ReferenceAxis = -> Sketch079 [N_Axis]
  Type = 0
FEATURE [Sketcher::SketchObject] Sketch080
  FullyConstrained = true
  MapMode = 5
  Placement = pos=(0,0,0) rot=(0.57735,0.57735,0.57735;2.0944rad)
  Support = -> [YZ_Plane006]
  sketch-geometry (15):
    g0: LineSegment StartX=-17 StartY=26 StartZ=0 EndX=-15 EndY=28 EndZ=0
    g1: LineSegment StartX=-11 StartY=28 StartZ=0 EndX=-9 EndY=26 EndZ=0
    g2: LineSegment StartX=-9 StartY=26 StartZ=0 EndX=-7 EndY=26 EndZ=0
    g3: LineSegment StartX=-7 StartY=26 StartZ=0 EndX=-5 EndY=28 EndZ=0
    g4: LineSegment StartX=-5 StartY=28 StartZ=0 EndX=5 EndY=28 EndZ=0
    g5: LineSegment StartX=5 StartY=28 StartZ=0 EndX=7 EndY=26 EndZ=0
    g6: LineSegment StartX=7 StartY=26 StartZ=0 EndX=9 EndY=26 EndZ=0
    g7: LineSegment StartX=9 StartY=26 StartZ=0 EndX=11 EndY=28 EndZ=0
    g8: LineSegment StartX=11 StartY=28 StartZ=0 EndX=15 EndY=28 EndZ=0
    g9: LineSegment StartX=15 StartY=28 StartZ=0 EndX=17 EndY=26 EndZ=0
    g10: LineSegment StartX=17 StartY=26 StartZ=0 EndX=17 EndY=32 EndZ=0
    g11: LineSegment StartX=17 StartY=32 StartZ=0 EndX=-17 EndY=32 EndZ=0
    g12: LineSegment StartX=-17 StartY=32 StartZ=0 EndX=-17 EndY=26 EndZ=0
    g13: LineSegment StartX=-15 StartY=28 StartZ=0 EndX=-13 EndY=28 EndZ=0
    g14: LineSegment StartX=-13 StartY=28 StartZ=0 EndX=-11 EndY=28 EndZ=0
  constraints (37):
    c: Coincident(g0,g13)
    c: Coincident(g14,g1)
    c: Coincident(g1,g2)
    c: Coincident(g2,g3)
    c: Coincident(g3,g4)
    c: Coincident(g4,g5)
    c: Coincident(g5,g6)
    c: Coincident(g6,g7)
    c: Coincident(g7,g8)
    c: Coincident(g8,g9)
    c: Coincident(g9,g10)
    c: Coincident(g10,g11)
    c: Coincident(g11,g12)
    c: Coincident(g12,g0)
    c: Vertical(g12)
    c: Symmetric(g11,g10,g-2)
    c: Symmetric(g0,g9,g-2)
    c: Symmetric(g0,g8,g-2)
    c: Angle(g0) = 0.785398
    c: Symmetric(g14,g7,g-2)
    c: Angle(g1) = -0.785398
    c: Symmetric(g1,g6,g-2)
    c: Horizontal(g2)
    c: Horizontal(g0,g1)
    c: Symmetric(g2,g5,g-2)
    c: Angle(g3) = 0.785398
    c: Symmetric(g3,g4,g-2)
    c: Coincident(g13,g14)
    c: Horizontal(g13)
    c: Symmetric(g0,g1,g13)
    c: DistanceX(g13,g-1) = 13
    c: Horizontal(g1,g3)
    c: DistanceY(g13) = 28
    c: DistanceX(g8,g8) = 4
    c: DistanceY(g0,g0) = 2
    c: DistanceX(g4,g4) = 10
    c: DistanceY(g12,g12) = 6
FEATURE [PartDesign::Pocket] Pocket026
  BaseFeature = -> Pad023
  Direction = (-1,2e-16,-3e-16)
  Length = 5
  Length2 = 5
  Midplane = true
  Profile = -> Sketch080
  ReferenceAxis = -> Sketch080 [N_Axis]
  Type = 1
FEATURE [PartDesign::Hole] Hole001
  BaseFeature = -> Pocket026
  CustomThreadClearance = 0
  Depth = 148.549
  DepthType = 1
  Diameter = 2.5
  DrillForDepth = false
  DrillPoint = 1
  DrillPointAngle = 118
  HoleCutCountersinkAngle = 90
  HoleCutCustomValues = false
  HoleCutDepth = 0
  HoleCutDiameter = 6.1
  HoleCutType = 0
  ModelThread = false
  Profile = -> Sketch006
  Reversed = true
  Tapered = false
  TaperedAngle = 90
  ThreadClass = 0
  ThreadDepth = 148.549
  ThreadDepthType = 0
  ThreadDirection = 0
  ThreadFit = 0
  ThreadSize = 9
  ThreadType = 1
  Threaded = true
  UseCustomThreadClearance = false
FEATURE [PartDesign::Hole] Hole003
  BaseFeature = -> Hole001
  CustomThreadClearance = 0
  Depth = 148.549
  DepthType = 1
  Diameter = 2.5
  DrillForDepth = false
  DrillPoint = 1
  DrillPointAngle = 118
  HoleCutCountersinkAngle = 90
  HoleCutCustomValues = false
  HoleCutDepth = 2.8
  HoleCutDiameter = 6
  HoleCutType = 0
  ModelThread = false
  Profile = -> Sketch010
  Reversed = true
  Tapered = false
  TaperedAngle = 90
  ThreadClass = 0
  ThreadDepth = 148.549
  ThreadDepthType = 0
  ThreadDirection = 0
  ThreadFit = 0
  ThreadSize = 9
  ThreadType = 1
  Threaded = true
  UseCustomThreadClearance = false
FEATURE [PartDesign::SubShapeBinder] Binder003
  BindCopyOnChange = 0
  BindMode = 0
  ClaimChildren = false
  Context = -> Part002 [Body001.Binder003.]
  Fuse = false
  MakeFace = true
  OffsetFill = false
  OffsetIntersection = false
  OffsetJoinType = 0
  OffsetOpenResult = false
  PartialLoad = false
  Placement = pos=(0,0,3) rot=(0,0,1;0rad)
  Relative = true
  Support = -> [Pad[Sketch.]]
  _Version = 2
FEATURE [PartDesign::Pad] Pad027
  BaseFeature = -> Hole003
  Direction = (0,0,1)
  Length = 0.2
  Length2 = 10
  Profile = -> Binder003
  Type = 0
FEATURE [PartDesign::Hole] Hole
  BaseFeature = -> Pad027
  CustomThreadClearance = 0
  Depth = 148.549
  DepthType = 1
  Diameter = 3.4
  DrillForDepth = false
  DrillPoint = 1
  DrillPointAngle = 118
  HoleCutCountersinkAngle = 90
  HoleCutCustomValues = false
  HoleCutDepth = 6
  HoleCutDiameter = 5.7
  HoleCutType = 1
  ModelThread = false
  Profile = -> Sketch005
  Tapered = false
  TaperedAngle = 90
  ThreadClass = 0
  ThreadDepth = 148.549
  ThreadDepthType = 0
  ThreadDirection = 0
  ThreadFit = 0
  ThreadSize = 9
  ThreadType = 1
  Threaded = false
  UseCustomThreadClearance = false
FEATURE [PartDesign::Hole] Hole002
  BaseFeature = -> Hole
  CustomThreadClearance = 0
  Depth = 148.549
  DepthType = 1
  Diameter = 3.4
  DrillForDepth = false
  DrillPoint = 1
  DrillPointAngle = 118
  HoleCutCountersinkAngle = 90
  HoleCutCustomValues = false
  HoleCutDepth = 0
  HoleCutDiameter = 6.1
  HoleCutType = 0
  ModelThread = false
  Profile = -> Sketch007
  Reversed = true
  Tapered = false
  TaperedAngle = 90
  ThreadClass = 0
  ThreadDepth = 148.549
  ThreadDepthType = 0
  ThreadDirection = 0
  ThreadFit = 0
  ThreadSize = 9
  ThreadType = 1
  Threaded = false
  UseCustomThreadClearance = false
FEATURE [PartDesign::Boolean] Boolean002
  BaseFeature = -> Hole002
  Refine = true
  Type = 1
FEATURE [PartDesign::Pad] Pad022
  BaseFeature = -> Boolean002
  Direction = (0,0,1)
  Length = 28
  Length2 = 10
  Profile = -> Sketch078
  ReferenceAxis = -> Sketch078 [N_Axis]
  Type = 0
FEATURE [PartDesign::Body] Body001  label="CarriageLeftMain"
  Group = -> [Sketch,Pad,Chamfer,Pad023,Pocket026,Hole001,Hole003,Binder003,Pad027,Hole,Hole002,Boolean002,Pad022,Sketch005,Sketch006,Sketch007,Sketch008,Sketch009,Sketch010,Sketch078,Sketch079,Sketch080]
  Origin = -> Origin006
  Tip = -> Boolean002
FEATURE [PartDesign::AdditiveBox] Box009
  AttacherType = Attacher::AttachEngine3D
  AttachmentOffset = pos=(-3,10,28) rot=(0,0,1;0rad)
  BaseFeature = -> Hole005
  Height = 0.2
  Length = 6
  MapMode = 2
  Placement = pos=(-3,10,28) rot=(0,0,1;0rad)
  Support = -> [Body001]
  Width = 6
FEATURE [PartDesign::AdditiveBox] Box010
  AttacherType = Attacher::AttachEngine3D
  AttachmentOffset = pos=(-3,-16,28) rot=(0,0,1;0rad)
  BaseFeature = -> Box009
  Height = 0.2
  Length = 6
  MapMode = 5
  Placement = pos=(-3,-16,28) rot=(0,0,1;0rad)
  Support = -> [XY_Plane008]
  Width = 6
FEATURE [PartDesign::AdditiveBox] Box011
  AttacherType = Attacher::AttachEngine3D
  AttachmentOffset = pos=(25,-3,28) rot=(0,0,1;0rad)
  BaseFeature = -> Box010
  Height = 0.2
  Length = 6
  MapMode = 5
  Placement = pos=(25,-3,28) rot=(0,0,1;0rad)
  Support = -> [XY_Plane008]
  Width = 6
FEATURE [PartDesign::Body] Body003  label="CarriageLeftBrace"
  Group = -> [Sketch011,Pad003,Box003,Box004,Box005,Fillet002,Fillet003,Chamfer001,Chamfer002,Sketch012,Hole004,Sketch013,Hole005,Box009,Box010,Box011]
  Origin = -> Origin008
  Tip = -> Box011
COMPONENT P6 — recipe-attached ("CarriageRight", modeled in this document).
Construction recipe (the document's own serialized feature program — sketch geometry with constraints, then the solid features built on it; lengths are millimeters unless a unit is written):

FEATURE [PartDesign::ShapeBinder] ShapeBinder002
  Support = -> [Sketch]
  TraceSupport = false
FEATURE [PartDesign::Pad] Pad024
  Direction = (0,0,1)
  Length = 7
  Length2 = 10
  Profile = -> ShapeBinder002
  Type = 0
FEATURE [PartDesign::Chamfer] Chamfer008
  Angle = 45
  Base = -> Pad024 [Face16]
  BaseFeature = -> Pad024
  ChamferType = 0
  FlipDirection = false
  Size = 1
  Size2 = 1
  SupportTransform = false
  UseAllEdges = false
FEATURE [Sketcher::SketchObject] Sketch081
  FullyConstrained = true
  MapMode = 5
  Support = -> [XY_Plane007]
  sketch-geometry (12):
    g0: LineSegment StartX=-1.25 StartY=5 StartZ=0 EndX=1.25 EndY=5 EndZ=0
    g1: LineSegment StartX=3.25 StartY=3 StartZ=0 EndX=3.25 EndY=-3 EndZ=0
    g2: LineSegment StartX=1.25 StartY=-5 StartZ=0 EndX=-1.25 EndY=-5 EndZ=0
    g3: LineSegment StartX=-3.25 StartY=-3 StartZ=0 EndX=-3.25 EndY=3 EndZ=0
    g4: ArcOfCircle CenterX=-1.25 CenterY=3 CenterZ=0 NormalX=0 NormalY=0 NormalZ=1 AngleXU=0 Radius=2 StartAngle=1.5708 EndAngle=3.14159
    g5: GeomPoint X=-3.25 Y=5 Z=0
    g6: ArcOfCircle CenterX=-1.25 CenterY=-3 CenterZ=0 NormalX=0 NormalY=0 NormalZ=1 AngleXU=0 Radius=2 StartAngle=3.14159 EndAngle=4.71239
    g7: GeomPoint X=-3.25 Y=-5 Z=0
    g8: ArcOfCircle CenterX=1.25 CenterY=-3 CenterZ=0 NormalX=0 NormalY=0 NormalZ=1 AngleXU=0 Radius=2 StartAngle=4.71239 EndAngle=6.28319
    g9: GeomPoint X=3.25 Y=-5 Z=0
    g10: ArcOfCircle CenterX=1.25 CenterY=3 CenterZ=0 NormalX=0 NormalY=0 NormalZ=1 AngleXU=0 Radius=2 StartAngle=0 EndAngle=1.5708
    g11: GeomPoint X=3.25 Y=5 Z=0
  constraints (25):
    c: Symmetric(g5,g11,g-2)
    c: Symmetric(g5,g7,g-1)
    c: Symmetric(g11,g9,g-1)
    c: DistanceX(g5,g11) = 6.5
    c: DistanceY(g7,g5) = 10
    c: PointOnObject(g5,g0)
    c: PointOnObject(g5,g3)
    c: Tangent(g0,g4) = 1.5708
    c: Tangent(g3,g4) = 1.5708
    c: PointOnObject(g7,g3)
    c: PointOnObject(g7,g2)
    c: Tangent(g3,g6) = 1.5708
    c: Tangent(g2,g6) = 1.5708
    c: PointOnObject(g9,g2)
    c: PointOnObject(g9,g1)
    c: Tangent(g2,g8) = 1.5708
    c: Tangent(g1,g8) = 1.5708
    c: PointOnObject(g11,g1)
    c: PointOnObject(g11,g0)
    c: Tangent(g1,g10) = 1.5708
    c: Tangent(g0,g10) = 1.5708
    c: Equal(g4,g6)
    c: Equal(g4,g8)
    c: Equal(g4,g10)
    c: Radius(g4) = 2
FEATURE [PartDesign::Pad] Pad025
  BaseFeature = -> Chamfer008
  Direction = (0,0,1)
  Length = 16.5
  Length2 = 10
  Profile = -> Sketch081
  ReferenceAxis = -> Sketch081 [N_Axis]
  Type = 0
FEATURE [PartDesign::ShapeBinder] ShapeBinder003
  Placement = pos=(0,0,0) rot=(0.57735,0.57735,0.57735;2.0944rad)
  Support = -> [Sketch080]
  TraceSupport = false
FEATURE [PartDesign::Pocket] Pocket027
  BaseFeature = -> Pad025
  Direction = (-1,0,0)
  Length = 5
  Length2 = 5
  Midplane = true
  Profile = -> ShapeBinder003
  Type = 1
FEATURE [PartDesign::ShapeBinder] ShapeBinder004
  Support = -> [Sketch006]
  TraceSupport = false
FEATURE [PartDesign::Hole] Hole027
  BaseFeature = -> Pocket027
  CustomThreadClearance = 0
  Depth = 141.346
  DepthType = 1
  Diameter = 2.5
  DrillForDepth = false
  DrillPoint = 1
  DrillPointAngle = 118
  HoleCutCountersinkAngle = 90
  HoleCutCustomValues = false
  HoleCutDepth = 0
  HoleCutDiameter = 6.1
  HoleCutType = 0
  ModelThread = false
  Profile = -> ShapeBinder004
  Reversed = true
  Tapered = false
  TaperedAngle = 90
  ThreadClass = 0
  ThreadDepth = 141.346
  ThreadDepthType = 0
  ThreadDirection = 0
  ThreadFit = 0
  ThreadSize = 9
  ThreadType = 1
  Threaded = true
  UseCustomThreadClearance = false
FEATURE [PartDesign::ShapeBinder] ShapeBinder005
  Support = -> [Sketch010]
  TraceSupport = false
FEATURE [PartDesign::Hole] Hole028
  BaseFeature = -> Hole027
  CustomThreadClearance = 0
  Depth = 25
  DepthType = 0
  Diameter = 2.5
  DrillForDepth = false
  DrillPoint = 1
  DrillPointAngle = 118
  HoleCutCountersinkAngle = 90
  HoleCutCustomValues = false
  HoleCutDepth = 0
  HoleCutDiameter = 6.1
  HoleCutType = 0
  ModelThread = false
  Profile = -> ShapeBinder005
  Reversed = true
  Tapered = false
  TaperedAngle = 90
  ThreadClass = 0
  ThreadDepth = 25
  ThreadDepthType = 0
  ThreadDirection = 0
  ThreadFit = 0
  ThreadSize = 9
  ThreadType = 1
  Threaded = true
  UseCustomThreadClearance = false
FEATURE [PartDesign::ShapeBinder] ShapeBinder006
  Placement = pos=(0,0,10) rot=(0,0,1;0rad)
  Support = -> [Sketch005]
  TraceSupport = false
FEATURE [PartDesign::ShapeBinder] ShapeBinder007
  Support = -> [Sketch007]
  TraceSupport = false
FEATURE [PartDesign::ShapeBinder] ShapeBinder014
  Support = -> [Sketch078]
  TraceSupport = false
FEATURE [PartDesign::SubShapeBinder] Binder004
  BindCopyOnChange = 0
  BindMode = 0
  ClaimChildren = false
  Context = -> Part003 [Body002.Binder004.]
  Fuse = false
  MakeFace = true
  OffsetFill = false
  OffsetIntersection = false
  OffsetJoinType = 0
  OffsetOpenResult = false
  PartialLoad = false
  Placement = pos=(0,0,3) rot=(0,0,1;0rad)
  Relative = true
  Support = -> [ShapeBinder002]
  _Version = 2
FEATURE [PartDesign::Pad] Pad028
  BaseFeature = -> Hole028
  Direction = (0,0,1)
  Length = 0.2
  Length2 = 10
  Profile = -> Binder004
  Type = 0
FEATURE [PartDesign::Hole] Hole029
  BaseFeature = -> Pad028
  CustomThreadClearance = 0
  Depth = 141.346
  DepthType = 1
  Diameter = 3.4
  DrillForDepth = false
  DrillPoint = 1
  DrillPointAngle = 118
  HoleCutCountersinkAngle = 90
  HoleCutCustomValues = false
  HoleCutDepth = 6
  HoleCutDiameter = 5.7
  HoleCutType = 1
  ModelThread = false
  Profile = -> ShapeBinder006
  Tapered = false
  TaperedAngle = 90
  ThreadClass = 0
  ThreadDepth = 141.346
  ThreadDepthType = 0
  ThreadDirection = 0
  ThreadFit = 0
  ThreadSize = 9
  ThreadType = 1
  Threaded = false
  UseCustomThreadClearance = false
FEATURE [PartDesign::Hole] Hole030
  BaseFeature = -> Hole029
  CustomThreadClearance = 0
  Depth = 141.346
  DepthType = 1
  Diameter = 3.4
  DrillForDepth = false
  DrillPoint = 1
  DrillPointAngle = 118
  HoleCutCountersinkAngle = 90
  HoleCutCustomValues = false
  HoleCutDepth = 0
  HoleCutDiameter = 6.1
  HoleCutType = 0
  ModelThread = false
  Profile = -> ShapeBinder007
  Reversed = true
  Tapered = false
  TaperedAngle = 90
  ThreadClass = 0
  ThreadDepth = 141.346
  ThreadDepthType = 0
  ThreadDirection = 0
  ThreadFit = 0
  ThreadSize = 9
  ThreadType = 1
  Threaded = false
  UseCustomThreadClearance = false
FEATURE [PartDesign::Boolean] Boolean003
  BaseFeature = -> Hole030
  Group = -> [ShapeBinder008,ShapeBinder009,ShapeBinder010,ShapeBinder011,ShapeBinder012,ShapeBinder013]
  Refine = true
  Type = 1
FEATURE [PartDesign::Pad] Pad026
  BaseFeature = -> Boolean003
  Direction = (0,0,1)
  Length = 28
  Length2 = 10
  Profile = -> ShapeBinder014
  Type = 0
FEATURE [PartDesign::Body] Body002  label="CarriageRightMain"
  Group = -> [ShapeBinder002,Pad024,Chamfer008,Sketch081,Pad025,ShapeBinder003,Pocket027,ShapeBinder004,Hole027,ShapeBinder005,Hole028,Binder004,Pad028,ShapeBinder006,Hole029,ShapeBinder007,Hole030,Boolean003,ShapeBinder014,Pad026]
  Origin = -> Origin007
  Tip = -> Boolean003
COMPONENT P7 — recipe-attached ("TopPanel", modeled in this document).
Construction recipe (the document's own serialized feature program — sketch geometry with constraints, then the solid features built on it; lengths are millimeters unless a unit is written):

FEATURE [Sketcher::SketchObject] Sketch014
  FullyConstrained = true
  MapMode = 2
  Placement = pos=(0,0,0) rot=(0,1,0;3.14159rad)
  Support = -> [XY_Plane010]
  expr: Constraints[5] = <<Variables>>.GantorySpacing / 2
  sketch-geometry (18):
    g0: Circle CenterX=-100 CenterY=0 CenterZ=0 NormalX=0 NormalY=0 NormalZ=1 AngleXU=0 Radius=3.2
    g1: Circle CenterX=100 CenterY=0 CenterZ=0 NormalX=0 NormalY=0 NormalZ=1 AngleXU=0 Radius=3.2
    g2: Circle CenterX=-100 CenterY=20 CenterZ=0 NormalX=0 NormalY=0 NormalZ=1 AngleXU=0 Radius=3.2
    g3: Circle CenterX=-100 CenterY=40 CenterZ=0 NormalX=0 NormalY=0 NormalZ=1 AngleXU=0 Radius=3.2
    g4: Circle CenterX=-100 CenterY=60 CenterZ=0 NormalX=0 NormalY=0 NormalZ=1 AngleXU=0 Radius=3.2
    g5: Circle CenterX=-100 CenterY=80 CenterZ=0 NormalX=0 NormalY=0 NormalZ=1 AngleXU=0 Radius=3.2
    g6: Circle CenterX=-100 CenterY=-20 CenterZ=0 NormalX=0 NormalY=0 NormalZ=1 AngleXU=0 Radius=3.2
    g7: Circle CenterX=-100 CenterY=-40 CenterZ=0 NormalX=0 NormalY=0 NormalZ=1 AngleXU=0 Radius=3.2
    g8: Circle CenterX=-100 CenterY=-60 CenterZ=0 NormalX=0 NormalY=0 NormalZ=1 AngleXU=0 Radius=3.2
    g9: Circle CenterX=-100 CenterY=-80 CenterZ=0 NormalX=0 NormalY=0 NormalZ=1 AngleXU=0 Radius=3.2
    g10: Circle CenterX=100 CenterY=20 CenterZ=0 NormalX=0 NormalY=0 NormalZ=1 AngleXU=0 Radius=3.2
    g11: Circle CenterX=100 CenterY=40 CenterZ=0 NormalX=0 NormalY=0 NormalZ=1 AngleXU=0 Radius=3.2
    g12: Circle CenterX=100 CenterY=60 CenterZ=0 NormalX=0 NormalY=0 NormalZ=1 AngleXU=0 Radius=3.2
    g13: Circle CenterX=100 CenterY=80 CenterZ=0 NormalX=0 NormalY=0 NormalZ=1 AngleXU=0 Radius=3.2
    g14: Circle CenterX=100 CenterY=-20 CenterZ=0 NormalX=0 NormalY=0 NormalZ=1 AngleXU=0 Radius=3.2
    g15: Circle CenterX=100 CenterY=-40 CenterZ=0 NormalX=0 NormalY=0 NormalZ=1 AngleXU=0 Radius=3.2
    g16: Circle CenterX=100 CenterY=-60 CenterZ=0 NormalX=0 NormalY=0 NormalZ=1 AngleXU=0 Radius=3.2
    g17: Circle CenterX=100 CenterY=-80 CenterZ=0 NormalX=0 NormalY=0 NormalZ=1 AngleXU=0 Radius=3.2
  constraints (25):
    c: PointOnObject(g0,g-1)
    c: Vertical(g0,g2)
    c: Vertical(g2,g3)
    c: Vertical(g3,g4)
    c: Vertical(g4,g5)
    c: DistanceX(g0,g-1) = 100
    c: Equal(g0, g1-g17) x17
    c: Diameter(g0) = 6.4
    c: Symmetric(g1,g0,g-2)
    c: Symmetric(g2,g10,g-2)
    c: Symmetric(g3,g11,g-2)
    c: Symmetric(g4,g12,g-2)
    c: Symmetric(g5,g13,g-2)
    c: Symmetric(g6,g14,g-2)
    c: Symmetric(g7,g15,g-2)
    c: Symmetric(g8,g16,g-2)
    c: Symmetric(g9,g17,g-2)
    c: DistanceY(g0,g2) = 20
    c: DistanceY(g2,g3) = 20
    c: DistanceY(g3,g4) = 20
    c: DistanceY(g4,g5) = 20
    c: Symmetric(g6,g2,g-1)
    c: Symmetric(g7,g3,g-1)
    c: Symmetric(g8,g4,g-1)
    c: Symmetric(g9,g5,g-1)
FEATURE [PartDesign::CoordinateSystem] Local_CS
  AttacherType = Attacher::AttachEngine3D
  AttachmentOffset = pos=(0,0,16) rot=(0,0,1;0rad)
  MapMode = 2
  Placement = pos=(0,0,16) rot=(0,0,1;0rad)
  Support = -> [X_Axis010]
FEATURE [Sketcher::SketchObject] Sketch022
  FullyConstrained = true
  MapMode = 5
  Placement = pos=(0,0,0) rot=(1,0,0;1.5708rad)
  Support = -> [XZ_Plane010]
  expr: Constraints[10] = <<Variables>>.TopThickness
  expr: Constraints[11] = <<Variables>>.GantorySpacing + <<Variables>>.CavitySpacingX * 2
  expr: Constraints[12] = <<Variables>>.GantorySpacing + <<Variables>>.CavitySpacingX * 2 + 4
  expr: Constraints[15] = <<Variables>>.GantorySpacing + <<Variables>>.CavitySpacingX * 2
  expr: Constraints[17] = <<Variables>>.GantorySpacing
  sketch-geometry (38):
    g0: LineSegment StartX=110 StartY=41.0294 StartZ=0 EndX=110 EndY=30.2426 EndZ=0
    g1: LineSegment StartX=108.757 StartY=10 StartZ=0 EndX=-108.757 EndY=10 EndZ=0
    g2: LineSegment StartX=-111.121 StartY=27.8787 StartZ=0 EndX=-110.879 EndY=28.1213 EndZ=0
    g3: LineSegment StartX=112 StartY=25.7574 StartZ=0 EndX=112 EndY=13.2426 EndZ=0
    g4: LineSegment StartX=111.121 StartY=11.1213 StartZ=0 EndX=110.879 EndY=10.8787 EndZ=0
    g5: LineSegment StartX=-112 StartY=13.2426 StartZ=0 EndX=-112 EndY=25.7574 EndZ=0
    g6: LineSegment StartX=-106.485 StartY=49.5147 StartZ=0 EndX=-101.757 EndY=54.2426 EndZ=0
    g7: LineSegment StartX=-100 StartY=60 StartZ=0 EndX=-100 EndY=58.4853 EndZ=0
    g8: LineSegment StartX=106.485 StartY=49.5147 StartZ=0 EndX=101.757 EndY=54.2426 EndZ=0
    g9: LineSegment StartX=100 StartY=60 StartZ=0 EndX=100 EndY=58.4853 EndZ=0
    g10: LineSegment StartX=110.879 StartY=28.1213 StartZ=0 EndX=111.121 EndY=27.8787 EndZ=0
    g11: LineSegment StartX=-110 StartY=30.2426 StartZ=0 EndX=-110 EndY=41.0294 EndZ=0
    g12: LineSegment StartX=-110.879 StartY=10.8787 StartZ=0 EndX=-111.121 EndY=11.1213 EndZ=0
    g13: ArcOfCircle CenterX=-98 CenterY=41.0294 CenterZ=0 NormalX=0 NormalY=0 NormalZ=1 AngleXU=0 Radius=12 StartAngle=2.35619 EndAngle=3.14159
    g14: GeomPoint X=-110 Y=46 Z=0
    g15: ArcOfCircle CenterX=98 CenterY=41.0294 CenterZ=0 NormalX=0 NormalY=0 NormalZ=1 AngleXU=0 Radius=12 StartAngle=-1.8e-15 EndAngle=0.785398
    g16: GeomPoint X=110 Y=46 Z=0
    g17: ArcOfCircle CenterX=113 CenterY=30.2426 CenterZ=0 NormalX=0 NormalY=0 NormalZ=1 AngleXU=0 Radius=3 StartAngle=3.14159 EndAngle=3.92699
    g18: GeomPoint X=110 Y=29 Z=0
    g19: ArcOfCircle CenterX=109 CenterY=25.7574 CenterZ=0 NormalX=0 NormalY=0 NormalZ=1 AngleXU=0 Radius=3 StartAngle=-9e-16 EndAngle=0.785398
    g20: GeomPoint X=112 Y=27 Z=0
    g21: ArcOfCircle CenterX=-113 CenterY=30.2426 CenterZ=0 NormalX=0 NormalY=0 NormalZ=1 AngleXU=0 Radius=3 StartAngle=5.49779 EndAngle=6.28319
    g22: GeomPoint X=-110 Y=29 Z=0
    g23: ArcOfCircle CenterX=-109 CenterY=25.7574 CenterZ=0 NormalX=0 NormalY=0 NormalZ=1 AngleXU=0 Radius=3 StartAngle=2.35619 EndAngle=3.14159
    g24: GeomPoint X=-112 Y=27 Z=0
    g25: ArcOfCircle CenterX=-109 CenterY=13.2426 CenterZ=0 NormalX=0 NormalY=0 NormalZ=1 AngleXU=0 Radius=3 StartAngle=3.14159 EndAngle=3.92699
    g26: GeomPoint X=-112 Y=12 Z=0
    g27: ArcOfCircle CenterX=-108.757 CenterY=13 CenterZ=0 NormalX=0 NormalY=0 NormalZ=1 AngleXU=0 Radius=3 StartAngle=3.92699 EndAngle=4.71239
    g28: GeomPoint X=-110 Y=10 Z=0
    g29: ArcOfCircle CenterX=109 CenterY=13.2426 CenterZ=0 NormalX=0 NormalY=0 NormalZ=1 AngleXU=0 Radius=3 StartAngle=5.49779 EndAngle=6.28319
    g30: GeomPoint X=112 Y=12 Z=0
    g31: ArcOfCircle CenterX=108.757 CenterY=13 CenterZ=0 NormalX=0 NormalY=0 NormalZ=1 AngleXU=0 Radius=3 StartAngle=4.71239 EndAngle=5.49779
    g32: GeomPoint X=110 Y=10 Z=0
    g33: ArcOfCircle CenterX=-106 CenterY=58.4853 CenterZ=0 NormalX=0 NormalY=0 NormalZ=1 AngleXU=0 Radius=6 StartAngle=5.49779 EndAngle=6.28319
    g34: GeomPoint X=-100 Y=56 Z=0
    g35: ArcOfCircle CenterX=106 CenterY=58.4853 CenterZ=0 NormalX=0 NormalY=0 NormalZ=1 AngleXU=0 Radius=6 StartAngle=3.14159 EndAngle=3.92699
    g36: GeomPoint X=100 Y=56 Z=0
    g37: LineSegment StartX=-100 StartY=60 StartZ=0 EndX=100 EndY=60 EndZ=0
  constraints (83):
    c: Symmetric(g28,g32,g-2)
    c: Symmetric(g26,g30,g-2)
    c: Symmetric(g24,g20,g-2)
    c: Symmetric(g22,g18,g-2)
    c: Symmetric(g14,g16,g-2)
    c: Symmetric(g34,g36,g-2)
    c: Symmetric(g7,g9,g-2)
    c: Vertical(g5)
    c: Vertical(g11)
    c: Vertical(g7)
    c: DistanceY(g-1,g28) = 10
    c: DistanceX(g28,g32) = 220
    c: DistanceX(g26,g30) = 224
    c: Angle(g12) = 2.35619
    c: Angle(g2) = 0.785398
    c: DistanceX(g22,g18) = 220
    c: Angle(g6) = 0.785398
    c: DistanceX(g7,g9) = 200
    c: DistanceY(g28,g22) = 19
    c: DistanceY(g-1,g7) = 60
    c: DistanceY(g28,g14) = 36
    c: PointOnObject(g14,g6)
    c: PointOnObject(g14,g11)
    c: Tangent(g6,g13) = 1.5708
    c: Tangent(g11,g13) = 1.5708
    c: PointOnObject(g16,g8)
    c: PointOnObject(g16,g0)
    c: Tangent(g8,g15) = -1.5708
    c: Tangent(g0,g15) = 1.5708
    c: Equal(g13,g15)
    c: Radius(g13) = 12
    c: PointOnObject(g18,g0)
    c: PointOnObject(g18,g10)
    c: Tangent(g0,g17) = -1.5708
    c: Tangent(g10,g17) = -1.5708
    c: PointOnObject(g20,g10)
    c: PointOnObject(g20,g3)
    c: Tangent(g10,g19) = 1.5708
    c: Tangent(g3,g19) = 1.5708
    c: PointOnObject(g22,g11)
    c: PointOnObject(g22,g2)
    c: Tangent(g11,g21) = -1.5708
    c: Tangent(g2,g21) = -1.5708
    c: PointOnObject(g24,g2)
    c: PointOnObject(g24,g5)
    c: Tangent(g2,g23) = 1.5708
    c: Tangent(g5,g23) = 1.5708
    c: Equal(g17,g19)
    c: Equal(g17,g21)
    c: Equal(g17,g23)
    c: Radius(g17) = 3
    c: PointOnObject(g26,g5)
    c: PointOnObject(g26,g12)
    c: Tangent(g5,g25) = 1.5708
    c: Tangent(g12,g25) = 1.5708
    c: PointOnObject(g28,g12)
    c: PointOnObject(g28,g1)
    c: Tangent(g12,g27) = 1.5708
    c: Tangent(g1,g27) = 1.5708
    c: PointOnObject(g30,g3)
    c: PointOnObject(g30,g4)
    c: Tangent(g3,g29) = 1.5708
    c: Tangent(g4,g29) = 1.5708
    c: PointOnObject(g32,g4)
    c: PointOnObject(g32,g1)
    c: Tangent(g4,g31) = 1.5708
    c: Tangent(g1,g31) = 1.5708
    c: Equal(g25,g27)
    c: Equal(g25,g29)
    c: Equal(g25,g31)
    c: Radius(g25) = 3
    c: PointOnObject(g34,g6)
    c: PointOnObject(g34,g7)
    c: Tangent(g6,g33) = -1.5708
    c: Tangent(g7,g33) = 1.5708
    c: PointOnObject(g36,g9)
    c: PointOnObject(g36,g8)
    c: Tangent(g9,g35) = -1.5708
    c: Tangent(g8,g35) = 1.5708
    c: Equal(g33,g35)
    c: Radius(g33) = 6
    c: Coincident(g37,g7)
    c: Coincident(g37,g9)
FEATURE [Sketcher::SketchObject] Sketch028
  FullyConstrained = true
  MapMode = 5
  Support = -> [XY_Plane010]
  expr: Constraints[24] = <<Variables>>.GantorySpacing
  expr: Constraints[25] = <<Variables>>.GantorySpacing
  expr: Constraints[26] = <<Variables>>.GantorySpacing + <<Variables>>.CavitySpacingX * 2
  expr: Constraints[27] = <<Variables>>.GantorySpacing + <<Variables>>.CavitySpacingY * 2
  sketch-geometry (32):
    g0: ArcOfCircle CenterX=-100 CenterY=-100 CenterZ=0 NormalX=0 NormalY=0 NormalZ=1 AngleXU=0 Radius=6 StartAngle=-9e-16 EndAngle=2.73056
    g1: LineSegment StartX=-94 StartY=-100 StartZ=0 EndX=-94 EndY=-109.5 EndZ=0
    g2: ArcOfCircle CenterX=100 CenterY=-100 CenterZ=0 NormalX=0 NormalY=0 NormalZ=1 AngleXU=0 Radius=6 StartAngle=0.411029 EndAngle=3.14159
    g3: ArcOfCircle CenterX=-100 CenterY=100 CenterZ=0 NormalX=0 NormalY=0 NormalZ=1 AngleXU=0 Radius=6 StartAngle=3.55262 EndAngle=6.28319
    g4: ArcOfCircle CenterX=100 CenterY=100 CenterZ=0 NormalX=0 NormalY=0 NormalZ=1 AngleXU=0 Radius=6 StartAngle=3.14159 EndAngle=5.87216
    g5: LineSegment StartX=94 StartY=-100 StartZ=0 EndX=94 EndY=-109.5 EndZ=0
    g6: LineSegment StartX=94 StartY=100 StartZ=0 EndX=94 EndY=107 EndZ=0
    g7: LineSegment StartX=-94 StartY=107 StartZ=0 EndX=-94 EndY=100 EndZ=0
    g8: LineSegment StartX=-110 StartY=110 StartZ=0 EndX=-91 EndY=110 EndZ=0
    g9: LineSegment StartX=-107.936 StartY=98.064 StartZ=0 EndX=-110 EndY=96 EndZ=0
    g10: LineSegment StartX=-110 StartY=96 StartZ=0 EndX=-110 EndY=110 EndZ=0
    g11: LineSegment StartX=110 StartY=110 StartZ=0 EndX=110 EndY=96 EndZ=0
    g12: LineSegment StartX=110 StartY=96 StartZ=0 EndX=107.936 EndY=98.064 EndZ=0
    g13: LineSegment StartX=91 StartY=110 StartZ=0 EndX=110 EndY=110 EndZ=0
    g14: LineSegment StartX=-110 StartY=-110 StartZ=0 EndX=-110 EndY=-96 EndZ=0
    g15: LineSegment StartX=-110 StartY=-96 StartZ=0 EndX=-107.936 EndY=-98.064 EndZ=0
    g16: LineSegment StartX=-94.5 StartY=-110 StartZ=0 EndX=-110 EndY=-110 EndZ=0
    g17: LineSegment StartX=110 StartY=-110 StartZ=0 EndX=110 EndY=-96 EndZ=0
    g18: LineSegment StartX=110 StartY=-96 StartZ=0 EndX=107.936 EndY=-98.064 EndZ=0
    g19: LineSegment StartX=94.5 StartY=-110 StartZ=0 EndX=110 EndY=-110 EndZ=0
    g20: ArcOfCircle CenterX=-106.875 CenterY=-97.0034 CenterZ=0 NormalX=0 NormalY=0 NormalZ=1 AngleXU=0 Radius=1.5 StartAngle=3.92699 EndAngle=5.87216
    g21: ArcOfCircle CenterX=-94.5 CenterY=-109.5 CenterZ=0 NormalX=0 NormalY=0 NormalZ=1 AngleXU=0 Radius=0.5 StartAngle=4.71239 EndAngle=6.28319
    g22: ArcOfCircle CenterX=-106.875 CenterY=97.0034 CenterZ=0 NormalX=0 NormalY=0 NormalZ=1 AngleXU=0 Radius=1.5 StartAngle=0.411029 EndAngle=2.35619
    g23: ArcOfCircle CenterX=-91 CenterY=107 CenterZ=0 NormalX=0 NormalY=0 NormalZ=1 AngleXU=0 Radius=3 StartAngle=1.5708 EndAngle=3.14159
    g24: ArcOfCircle CenterX=91 CenterY=107 CenterZ=0 NormalX=0 NormalY=0 NormalZ=1 AngleXU=0 Radius=3 StartAngle=1.5e-15 EndAngle=1.5708
    g25: ArcOfCircle CenterX=106.875 CenterY=97.0034 CenterZ=0 NormalX=0 NormalY=0 NormalZ=1 AngleXU=0 Radius=1.5 StartAngle=0.785398 EndAngle=2.73056
    g26: ArcOfCircle CenterX=94.5 CenterY=-109.5 CenterZ=0 NormalX=0 NormalY=0 NormalZ=1 AngleXU=0 Radius=0.5 StartAngle=3.14159 EndAngle=4.71239
    g27: ArcOfCircle CenterX=106.875 CenterY=-97.0034 CenterZ=0 NormalX=0 NormalY=0 NormalZ=1 AngleXU=0 Radius=1.5 StartAngle=3.55262 EndAngle=5.49779
    g28: Circle CenterX=-100 CenterY=100 CenterZ=0 NormalX=0 NormalY=0 NormalZ=1 AngleXU=0 Radius=1.25
    g29: Circle CenterX=100 CenterY=100 CenterZ=0 NormalX=0 NormalY=0 NormalZ=1 AngleXU=0 Radius=1.25
    g30: Circle CenterX=-100 CenterY=-100 CenterZ=0 NormalX=0 NormalY=0 NormalZ=1 AngleXU=0 Radius=1.25
    g31: Circle CenterX=100 CenterY=-100 CenterZ=0 NormalX=0 NormalY=0 NormalZ=1 AngleXU=0 Radius=1.25
  constraints (68):
    c: Coincident(g9,g10)
    c: Coincident(g10,g8)
    c: Coincident(g11,g12)
    c: Coincident(g13,g11)
    c: Coincident(g14,g15)
    c: Coincident(g16,g14)
    c: Coincident(g17,g18)
    c: Coincident(g19,g17)
    c: Tangent(g20,g15) = -1.5708
    c: Tangent(g20,g0) = 1.5708
    c: Tangent(g22,g3) = 1.5708
    c: Tangent(g9,g22) = -1.5708
    c: Tangent(g8,g23) = 1.5708
    c: Tangent(g23,g7) = -1.5708
    c: Tangent(g24,g13) = 1.5708
    c: Tangent(g24,g6) = -1.5708
    c: Tangent(g12,g25) = -1.5708
    c: Tangent(g25,g4) = 1.5708
    c: Tangent(g18,g27) = 1.5708
    c: Tangent(g27,g2) = 1.5708
    c: Tangent(g2,g5) = -1.5708
    c: Tangent(g3,g7) = 1.5708
    c: Tangent(g4,g6) = 1.5708
    c: Tangent(g0,g1) = 1.5708
    c: DistanceX(g0,g2) = 200
    c: DistanceY(g0,g3) = 200
    c: DistanceX(g14,g17) = 220
    c: DistanceY(g14,g8) = 220
    c: Angle(g15) = -0.785398
    c: DistanceY(g14,g14) = 14
    c: Vertical(g14)
    c: Horizontal(g16)
    c: Vertical(g1)
    c: Diameter(g0) = 12
    c: Diameter(g20) = 3
    c: Diameter(g21) = 1
    c: Symmetric(g14,g17,g-2)
    c: Symmetric(g14,g8,g-1)
    c: Symmetric(g14,g11,g-1)
    c: Symmetric(g14,g17,g-2)
    c: Symmetric(g14,g9,g-1)
    c: Symmetric(g14,g11,g-1)
    c: Symmetric(g0,g2,g-2)
    c: Symmetric(g0,g3,g-1)
    c: Symmetric(g0,g4,g-1)
    c: Symmetric(g16,g19,g-2)
    c: Symmetric(g15,g18,g-2)
    c: Symmetric(g15,g9,g-1)
    c: Symmetric(g15,g12,g-1)
    c: Symmetric(g1,g5,g-2)
    c: Diameter(g23) = 6
    c: Tangent(g21,g16) = 1.5708
    c: Tangent(g21,g1) = 1.5708
    c: Tangent(g26,g19) = -1.5708
    c: Tangent(g26,g5) = -1.5708
    c: Symmetric(g8,g13,g-2)
    c: Symmetric(g7,g6,g-2)
    c: Vertical(g7)
    c: Horizontal(g8)
    c: Equal(g0,g3)
    c: Coincident(g28,g3)
    c: Coincident(g29,g4)
    c: Coincident(g30,g0)
    c: Coincident(g31,g2)
    c: Equal(g28,g29)
    c: Equal(g28,g30)
    c: Equal(g28,g31)
    c: Diameter(g28) = 2.5
FEATURE [Sketcher::SketchObject] Sketch030
  AttachmentOffset = pos=(0,0,60) rot=(0,0,1;0rad)
  FullyConstrained = true
  MapMode = 5
  Placement = pos=(0,0,60) rot=(0,0,1;0rad)
  Support = -> [XY_Plane010]
  expr: Constraints[14] = <<Variables>>.GantorySpacing + <<Variables>>.CavitySpacingX * 2
  expr: Constraints[23] = Variables.GantorySpacing + (<<Variables>>.CavitySpacingX + <<Variables>>.WallThickness) * 2
  expr: Constraints[24] = <<Variables>>.GantorySpacing / 2 + <<Variables>>.CavitySpacingY
  expr: Constraints[41] = Variables.GantorySpacing / 2 - 6
  expr: Constraints[49] = <<Variables>>.WallThickness
  sketch-geometry (22):
    g0: LineSegment StartX=-110 StartY=122 StartZ=0 EndX=-76.5 EndY=122 EndZ=0
    g1: LineSegment StartX=110 StartY=94 StartZ=0 EndX=-110 EndY=94 EndZ=0
    g2: LineSegment StartX=-110 StartY=94 StartZ=0 EndX=-110 EndY=122 EndZ=0
    g3: LineSegment StartX=76.5 StartY=122 StartZ=0 EndX=110 EndY=122 EndZ=0
    g4: LineSegment StartX=110 StartY=122 StartZ=0 EndX=110 EndY=94 EndZ=0
    g5: LineSegment StartX=-27 StartY=110 StartZ=0 EndX=27 EndY=110 EndZ=0
    g6: LineSegment StartX=27 StartY=110 StartZ=0 EndX=27 EndY=100 EndZ=0
    g7: LineSegment StartX=-27 StartY=100 StartZ=0 EndX=-27 EndY=110 EndZ=0
    g8: LineSegment StartX=-117 StartY=110 StartZ=0 EndX=117 EndY=110 EndZ=0
    g9: LineSegment StartX=-117 StartY=100 StartZ=0 EndX=117 EndY=100 EndZ=0
    g10: LineSegment StartX=-77 StartY=116.5 StartZ=0 EndX=-77 EndY=110 EndZ=0
    g11: LineSegment StartX=-77 StartY=110 StartZ=0 EndX=-53 EndY=110 EndZ=0
    g12: LineSegment StartX=-53 StartY=110 StartZ=0 EndX=-53 EndY=100 EndZ=0
    g13: LineSegment StartX=-53 StartY=100 StartZ=0 EndX=-27 EndY=100 EndZ=0
    g14: LineSegment StartX=27 StartY=100 StartZ=0 EndX=53 EndY=100 EndZ=0
    g15: LineSegment StartX=53 StartY=100 StartZ=0 EndX=53 EndY=110 EndZ=0
    g16: LineSegment StartX=53 StartY=110 StartZ=0 EndX=77 EndY=110 EndZ=0
    g17: LineSegment StartX=76.5 StartY=117 StartZ=0 EndX=76.5 EndY=122 EndZ=0
    g18: ArcOfCircle CenterX=-76.5 CenterY=116.5 CenterZ=0 NormalX=0 NormalY=0 NormalZ=1 AngleXU=0 Radius=0.5 StartAngle=1.5708 EndAngle=3.14159
    g19: LineSegment StartX=-76.5 StartY=122 StartZ=0 EndX=-76.5 EndY=117 EndZ=0
    g20: ArcOfCircle CenterX=76.5 CenterY=116.5 CenterZ=0 NormalX=0 NormalY=0 NormalZ=1 AngleXU=0 Radius=0.5 StartAngle=9e-16 EndAngle=1.5708
    g21: LineSegment StartX=77 StartY=110 StartZ=0 EndX=77 EndY=116.5 EndZ=0
  constraints (57):
    c: Coincident(g1,g2)
    c: Coincident(g2,g0)
    c: Horizontal(g0)
    c: Vertical(g2)
    c: Coincident(g3,g4)
    c: Coincident(g17,g3)
    c: Coincident(g5,g6)
    c: Coincident(g7,g5)
    c: Symmetric(g5,g5,g-2)
    c: Vertical(g7)
    c: Symmetric(g7,g6,g-2)
    c: Symmetric(g0,g3,g-2)
    c: Symmetric(g0,g3,g-2)
    c: Symmetric(g1,g4,g-2)
    c: DistanceX(g0,g3) = 220
    c: DistanceX(g5,g5) = 54
    c: Coincident(g1,g4)
    c: Coincident(g12,g11)
    c: Coincident(g13,g7)
    c: Coincident(g14,g6)
    c: Coincident(g15,g16)
    c: Symmetric(g11,g16,g-2)
    c: Symmetric(g8,g8,g-2)
    c: DistanceX(g8,g8) = 234
    c: DistanceY(g8) = 110
    c: Symmetric(g9,g9,g-2)
    c: Equal(g8,g9)
    c: DistanceY(g9,g8) = 10
    c: PointOnObject(g5,g8)
    c: Coincident(g10,g11)
    c: Vertical(g10)
    c: Coincident(g12,g13)
    c: Coincident(g14,g15)
    c: PointOnObject(g10,g8)
    c: PointOnObject(g11,g8)
    c: Vertical(g12)
    c: Symmetric(g10,g16,g-2)
    c: Symmetric(g12,g14,g-2)
    c: DistanceX(g11,g11) = 24
    c: PointOnObject(g12,g9)
    c: PointOnObject(g7,g9)
    c: DistanceY(g1) = 94
    c: DistanceX(g1,g10) = 33
    c: Tangent(g18,g10) = -1.5708
    c: Coincident(g19,g0)
    c: Vertical(g19)
    c: PointOnObject(g18,g19)
    c: Coincident(g18,g19)
    c: Diameter(g18) = 1
    c: DistanceY(g10,g18) = 7
    c: DistanceY(g19,g19) = 5
    c: Coincident(g20,g17)
    c: Coincident(g21,g16)
    c: Tangent(g21,g20) = -1.5708
    c: PointOnObject(g20,g17)
    c: Symmetric(g18,g20,g-2)
    c: Equal(g20,g18)
FEATURE [Sketcher::SketchObject] Sketch031
  AttachmentOffset = pos=(0,0,-117) rot=(0,0,1;0rad)
  FullyConstrained = true
  MapMode = 5
  Placement = pos=(0,117,2.6e-14) rot=(1,0,0;1.5708rad)
  Support = -> [XZ_Plane010]
  expr: .AttachmentOffset.Base.z = -(<<Variables>>.GantorySpacing / 2 + Variables.CavitySpacingY + <<Variables>>.WallThickness)
  expr: Constraints[26] = <<Variables>>.GantorySpacing + <<Variables>>.CavitySpacingX * 2
  expr: Constraints[68] = <<Variables>>.PullyDiameterDrive + <<Variables>>.PullyDiameterIdler
  sketch-geometry (39):
    g0: LineSegment StartX=-110 StartY=100 StartZ=0 EndX=-110 EndY=60 EndZ=0
    g1: LineSegment StartX=-110 StartY=60 StartZ=0 EndX=-50 EndY=60 EndZ=0
    g2: LineSegment StartX=-50 StartY=60 StartZ=0 EndX=-44.2265 EndY=50 EndZ=0
    g3: LineSegment StartX=-44.2265 StartY=50 StartZ=0 EndX=-35.7735 EndY=50 EndZ=0
    g4: LineSegment StartX=-35.7735 StartY=50 StartZ=0 EndX=-30 EndY=60 EndZ=0
    g5: LineSegment StartX=-30 StartY=60 StartZ=0 EndX=30 EndY=60 EndZ=0
    g6: LineSegment StartX=30 StartY=60 StartZ=0 EndX=35.7735 EndY=50 EndZ=0
    g7: LineSegment StartX=35.7735 StartY=50 StartZ=0 EndX=44.2265 EndY=50 EndZ=0
    g8: LineSegment StartX=44.2265 StartY=50 StartZ=0 EndX=50 EndY=60 EndZ=0
    g9: LineSegment StartX=50 StartY=60 StartZ=0 EndX=110 EndY=60 EndZ=0
    g10: LineSegment StartX=110 StartY=60 StartZ=0 EndX=110 EndY=100 EndZ=0
    g11: LineSegment StartX=110 StartY=100 StartZ=0 EndX=-110 EndY=100 EndZ=0
    g12: Circle CenterX=0 CenterY=55 CenterZ=0 NormalX=0 NormalY=0 NormalZ=1 AngleXU=0 Radius=1.25
    g13: Circle CenterX=-40 CenterY=55 CenterZ=0 NormalX=0 NormalY=0 NormalZ=1 AngleXU=0 Radius=1.25
    g14: Circle CenterX=40 CenterY=55 CenterZ=0 NormalX=0 NormalY=0 NormalZ=1 AngleXU=0 Radius=1.25
    g15: Circle CenterX=12.73 CenterY=50 CenterZ=0 NormalX=0 NormalY=0 NormalZ=1 AngleXU=0 Radius=1.25
    g16: Circle CenterX=-12.73 CenterY=50 CenterZ=0 NormalX=0 NormalY=0 NormalZ=1 AngleXU=0 Radius=1.25
    g17: Circle CenterX=-65 CenterY=55 CenterZ=0 NormalX=0 NormalY=0 NormalZ=1 AngleXU=0 Radius=1.25
    g18: Circle CenterX=65 CenterY=55 CenterZ=0 NormalX=0 NormalY=0 NormalZ=1 AngleXU=0 Radius=1.25
    g19: Circle CenterX=-15.9 CenterY=40 CenterZ=0 NormalX=0 NormalY=0 NormalZ=1 AngleXU=0 Radius=1.25
    g20: Circle CenterX=15.9 CenterY=40 CenterZ=0 NormalX=0 NormalY=0 NormalZ=1 AngleXU=0 Radius=1.25
    g21: LineSegment StartX=-117.5 StartY=55 StartZ=0 EndX=117.5 EndY=55 EndZ=0
    g22: LineSegment StartX=-117.5 StartY=45.9 StartZ=0 EndX=117.5 EndY=45.9 EndZ=0
    g23: LineSegment StartX=-15.9 StartY=0 StartZ=0 EndX=-15.9 EndY=100 EndZ=0
    g24: LineSegment StartX=15.9 StartY=0 StartZ=0 EndX=15.9 EndY=100 EndZ=0
    g25: LineSegment StartX=-65 StartY=0 StartZ=0 EndX=-65 EndY=100 EndZ=0
    g26: LineSegment StartX=65 StartY=0 StartZ=0 EndX=65 EndY=100 EndZ=0
    g27: LineSegment StartX=-12.73 StartY=0 StartZ=0 EndX=-12.73 EndY=100 EndZ=0
    g28: LineSegment StartX=12.73 StartY=0 StartZ=0 EndX=12.73 EndY=100 EndZ=0
    g29: LineSegment StartX=-117.5 StartY=30 StartZ=0 EndX=117.5 EndY=30 EndZ=0
    g30: Circle CenterX=-15.9 CenterY=30 CenterZ=0 NormalX=0 NormalY=0 NormalZ=1 AngleXU=0 Radius=1.25
    g31: Circle CenterX=15.9 CenterY=30 CenterZ=0 NormalX=0 NormalY=0 NormalZ=1 AngleXU=0 Radius=1.25
    g32: Circle CenterX=-15.9 CenterY=45.9 CenterZ=0 NormalX=0 NormalY=0 NormalZ=1 AngleXU=0 Radius=1.25
    g33: Circle CenterX=15.9 CenterY=45.9 CenterZ=0 NormalX=0 NormalY=0 NormalZ=1 AngleXU=0 Radius=1.25
    g34: LineSegment StartX=-117.5 StartY=40 StartZ=0 EndX=117.5 EndY=40 EndZ=0
    g35: Circle CenterX=-70 CenterY=40 CenterZ=0 NormalX=0 NormalY=0 NormalZ=1 AngleXU=0 Radius=1.25
    g36: Circle CenterX=70 CenterY=40 CenterZ=0 NormalX=0 NormalY=0 NormalZ=1 AngleXU=0 Radius=1.25
    g37: LineSegment StartX=-70 StartY=100 StartZ=0 EndX=-70 EndY=0 EndZ=0
    g38: LineSegment StartX=70 StartY=100 StartZ=0 EndX=70 EndY=0 EndZ=0
  constraints (104):
    c: Vertical(g0)
    c: Coincident(g0,g1)
    c: Coincident(g2,g3)
    c: Coincident(g3,g4)
    c: Coincident(g4,g5)
    c: Coincident(g5,g6)
    c: Coincident(g6,g7)
    c: Coincident(g7,g8)
    c: Coincident(g9,g10)
    c: Coincident(g10,g11)
    c: Coincident(g11,g0)
    c: Horizontal(g1)
    c: Horizontal(g3)
    c: Symmetric(g4,g5,g-2)
    c: Symmetric(g3,g6,g-2)
    c: Symmetric(g2,g7,g-2)
    c: Symmetric(g2,g8,g-2)
    c: Symmetric(g0,g9,g-2)
    c: Symmetric(g0,g10,g-2)
    c: DistanceX(g5,g5) = 60
    c: Horizontal(g4,g2)
    c: Angle(g4) = 1.0472
    c: Angle(g2) = -1.0472
    c: DistanceX(g2,g4) = 20
    c: DistanceY(g-1,g4) = 60
    c: DistanceY(g-1,g0) = 100
    c: DistanceX(g11,g11) = 220
    c: DistanceY(g3,g4) = 10
    c: PointOnObject(g12,g-2)
    c: Symmetric(g13,g14,g-2)
    c: DistanceX(g13,g14) = 80
    c: Equal(g12,g13)
    c: Equal(g12,g14)
    c: Diameter(g12) = 2.5
    c: Symmetric(g16,g15,g-2)
    c: DistanceY(g16) = 50
    c: Equal(g15,g16)
    c: Diameter(g15) = 2.5
    c: Symmetric(g17,g18,g-2)
    c: Equal(g17,g18)
    c: Diameter(g17) = 2.5
    c: Symmetric(g19,g20,g-2)
    c: Coincident(g1,g2)
    c: Coincident(g9,g8)
    c: Symmetric(g21,g21,g-2)
    c: Symmetric(g22,g22,g-2)
    c: PointOnObject(g23,g-1)
    c: Vertical(g23)
    c: PointOnObject(g25,g-1)
    c: Vertical(g25)
    c: Symmetric(g23,g24,g-2)
    c: Symmetric(g23,g24,g-2)
    c: DistanceY(g23,g23) = 100
    c: Symmetric(g25,g26,g-2)
    c: Symmetric(g25,g26,g-2)
    c: Equal(g23,g25)
    c: DistanceX(g23,g24) = 31.8
    c: DistanceX(g25,g26) = 130
    c: DistanceY(g21) = 55
    c: DistanceY(g22) = 45.9
    c: PointOnObject(g13,g21)
    c: PointOnObject(g12,g21)
    c: PointOnObject(g17,g21)
    c: PointOnObject(g17,g25)
    c: PointOnObject(g27,g-1)
    c: Vertical(g27)
    c: Symmetric(g27,g28,g-2)
    c: Symmetric(g27,g28,g-2)
    c: DistanceX(g27,g28) = 25.46
    c: Equal(g27,g23)
    c: PointOnObject(g16,g27)
    c: DistanceX(g22,g22) = 235
    c: Equal(g22,g21)
    c: Symmetric(g29,g29,g-2)
    c: Equal(g22,g29)
    c: DistanceY(g29) = 30
    c: Equal(g17,g19)
    c: Equal(g17,g20)
    c: Equal(g32,g12)
    c: Equal(g12,g33)
    c: Equal(g12,g30)
    c: Equal(g12,g31)
    c: Symmetric(g32,g33,g-2)
    c: Symmetric(g30,g31,g-2)
    c: PointOnObject(g30,g23)
    c: PointOnObject(g32,g23)
    c: PointOnObject(g30,g29)
    c: PointOnObject(g32,g22)
    c: PointOnObject(g19,g23)
    c: Symmetric(g34,g34,g-2)
    c: Equal(g34,g22)
    c: DistanceY(g34) = 40
    c: PointOnObject(g19,g34)
    c: PointOnObject(g35,g34)
    c: Symmetric(g35,g36,g-2)
    c: Equal(g35,g16)
    c: Equal(g36,g12)
    c: PointOnObject(g37,g11)
    c: PointOnObject(g37,g-1)
    c: Vertical(g37)
    c: Symmetric(g37,g38,g-2)
    c: Symmetric(g37,g38,g-2)
    c: DistanceX(g37,g38) = 140
    c: PointOnObject(g35,g37)
FEATURE [Sketcher::SketchObject] Sketch032
  AttachmentOffset = pos=(0,0,45) rot=(0,0,1;0rad)
  FullyConstrained = true
  MapMode = 5
  Placement = pos=(0,0,45) rot=(0,0,1;0rad)
  Support = -> [XY_Plane010]
  expr: Constraints[25] = <<Variables>>.GantorySpacing / 2 + <<Variables>>.CavitySpacingY - 4
  expr: Constraints[26] = <<Variables>>.GantorySpacing
  expr: Constraints[8] = <<Variables>>.GantorySpacing + <<Variables>>.CavitySpacingX * 2 - 10
  sketch-geometry (18):
    g0: Circle CenterX=-48 CenterY=106 CenterZ=0 NormalX=0 NormalY=0 NormalZ=1 AngleXU=0 Radius=2.5
    g1: Circle CenterX=-32 CenterY=106 CenterZ=0 NormalX=0 NormalY=0 NormalZ=1 AngleXU=0 Radius=2.5
    g2: Circle CenterX=48 CenterY=106 CenterZ=0 NormalX=0 NormalY=0 NormalZ=1 AngleXU=0 Radius=2.5
    g3: Circle CenterX=32 CenterY=106 CenterZ=0 NormalX=0 NormalY=0 NormalZ=1 AngleXU=0 Radius=2.5
    g4: Circle CenterX=-105 CenterY=9 CenterZ=0 NormalX=0 NormalY=0 NormalZ=1 AngleXU=0 Radius=2.5
    g5: Circle CenterX=-105 CenterY=-39 CenterZ=0 NormalX=0 NormalY=0 NormalZ=1 AngleXU=0 Radius=2.5
    g6: Circle CenterX=105 CenterY=9 CenterZ=0 NormalX=0 NormalY=0 NormalZ=1 AngleXU=0 Radius=2.5
    g7: Circle CenterX=105 CenterY=-39 CenterZ=0 NormalX=0 NormalY=0 NormalZ=1 AngleXU=0 Radius=2.5
    g8: Circle CenterX=105 CenterY=-72 CenterZ=0 NormalX=0 NormalY=0 NormalZ=1 AngleXU=0 Radius=2.5
    g9: Circle CenterX=105 CenterY=72 CenterZ=0 NormalX=0 NormalY=0 NormalZ=1 AngleXU=0 Radius=2.5
    g10: Circle CenterX=-105 CenterY=72 CenterZ=0 NormalX=0 NormalY=0 NormalZ=1 AngleXU=0 Radius=2.5
    g11: Circle CenterX=-105 CenterY=-72 CenterZ=0 NormalX=0 NormalY=0 NormalZ=1 AngleXU=0 Radius=2.5
    g12: LineSegment StartX=-100 StartY=106 StartZ=0 EndX=100 EndY=106 EndZ=0
    g13: GeomPoint X=-40 Y=106 Z=0
    g14: GeomPoint X=40 Y=106 Z=0
    g15: LineSegment StartX=-100 StartY=-15 StartZ=0 EndX=100 EndY=-15 EndZ=0
    g16: Circle CenterX=-105 CenterY=39 CenterZ=0 NormalX=0 NormalY=0 NormalZ=1 AngleXU=0 Radius=2.5
    g17: Circle CenterX=105 CenterY=39 CenterZ=0 NormalX=0 NormalY=0 NormalZ=1 AngleXU=0 Radius=2.5
  constraints (30):
    c: Symmetric(g1,g3,g-2)
    c: Symmetric(g0,g2,g-2)
    c: Symmetric(g10,g9,g-2)
    c: Symmetric(g4,g6,g-2)
    c: Symmetric(g5,g7,g-2)
    c: Symmetric(g11,g8,g-2)
    c: Symmetric(g10,g11,g-1)
    c: Vertical(g10,g4)
    c: DistanceX(g4,g6) = 210
    c: DistanceY(g5,g4) = 48
    c: DistanceY(g11,g10) = 144
    c: DistanceX(g0,g1) = 16
    c: Equal(g0, g1-g11) x11
    c: Diameter(g0) = 5
    c: Symmetric(g12,g12,g-2)
    c: DistanceY(g12) = 106
    c: DistanceX(g12,g12) = 200
    c: PointOnObject(g13,g12)
    c: Symmetric(g13,g14,g-2)
    c: DistanceX(g13,g14) = 80
    c: Symmetric(g0,g1,g13)
    c: PointOnObject(g0,g12)
    c: Symmetric(g15,g15,g-2)
    c: Equal(g15,g12)
    c: Symmetric(g4,g5,g15)
    c: DistanceY(g15) = -15
    c: Equal(g16,g0)
    c: Equal(g0,g17)
    c: Symmetric(g16,g17,g-2)
    c: Symmetric(g5,g16,g-1)
FEATURE [Sketcher::SketchObject] Sketch033
  AttachmentOffset = pos=(0,0,60) rot=(0,0,1;0rad)
  FullyConstrained = true
  MapMode = 5
  Placement = pos=(0,0,60) rot=(0,0,1;0rad)
  Support = -> [XY_Plane010]
  expr: Constraints[32] = <<Variables>>.GantorySpacing + (<<Variables>>.CavitySpacingY + <<Variables>>.WallThickness) * 2
  expr: Constraints[33] = <<Variables>>.GantorySpacing + (<<Variables>>.CavitySpacingX + <<Variables>>.WallThickness) * 2
  expr: Constraints[34] = Variables.GantorySpacing - 10
  expr: Constraints[35] = <<Variables>>.GantorySpacing + <<Variables>>.CavitySpacingY * 2 - 20
  sketch-geometry (16):
    g0: LineSegment StartX=-117 StartY=-100 StartZ=0 EndX=-95 EndY=-100 EndZ=0
    g1: LineSegment StartX=-95 StartY=-100 StartZ=0 EndX=-95 EndY=-117 EndZ=0
    g2: LineSegment StartX=-95 StartY=-117 StartZ=0 EndX=-117 EndY=-117 EndZ=0
    g3: LineSegment StartX=-117 StartY=-117 StartZ=0 EndX=-117 EndY=-100 EndZ=0
    g4: LineSegment StartX=95 StartY=-100 StartZ=0 EndX=117 EndY=-100 EndZ=0
    g5: LineSegment StartX=117 StartY=-100 StartZ=0 EndX=117 EndY=-117 EndZ=0
    g6: LineSegment StartX=117 StartY=-117 StartZ=0 EndX=95 EndY=-117 EndZ=0
    g7: LineSegment StartX=95 StartY=-117 StartZ=0 EndX=95 EndY=-100 EndZ=0
    g8: LineSegment StartX=95 StartY=117 StartZ=0 EndX=117 EndY=117 EndZ=0
    g9: LineSegment StartX=117 StartY=117 StartZ=0 EndX=117 EndY=100 EndZ=0
    g10: LineSegment StartX=117 StartY=100 StartZ=0 EndX=95 EndY=100 EndZ=0
    g11: LineSegment StartX=95 StartY=100 StartZ=0 EndX=95 EndY=117 EndZ=0
    g12: LineSegment StartX=-117 StartY=100 StartZ=0 EndX=-95 EndY=100 EndZ=0
    g13: LineSegment StartX=-95 StartY=100 StartZ=0 EndX=-95 EndY=117 EndZ=0
    g14: LineSegment StartX=-95 StartY=117 StartZ=0 EndX=-117 EndY=117 EndZ=0
    g15: LineSegment StartX=-117 StartY=117 StartZ=0 EndX=-117 EndY=100 EndZ=0
  constraints (36):
    c: Coincident(g0,g1)
    c: Coincident(g1,g2)
    c: Coincident(g2,g3)
    c: Coincident(g3,g0)
    c: Horizontal(g0)
    c: Horizontal(g2)
    c: Vertical(g1)
    c: Vertical(g3)
    c: Coincident(g4,g5)
    c: Coincident(g5,g6)
    c: Coincident(g6,g7)
    c: Coincident(g7,g4)
    c: Coincident(g8,g9)
    c: Coincident(g9,g10)
    c: Coincident(g10,g11)
    c: Coincident(g11,g8)
    c: Coincident(g12,g13)
    c: Coincident(g13,g14)
    c: Coincident(g14,g15)
    c: Coincident(g15,g12)
    c: Symmetric(g0,g12,g-1)
    c: Symmetric(g12,g0,g-1)
    c: Symmetric(g2,g14,g-1)
    c: Symmetric(g1,g13,g-1)
    c: Symmetric(g0,g4,g-2)
    c: Symmetric(g1,g6,g-2)
    c: Symmetric(g0,g4,g-2)
    c: Symmetric(g2,g5,g-2)
    c: Symmetric(g0,g10,g-1)
    c: Symmetric(g0,g9,g-1)
    c: Symmetric(g1,g8,g-1)
    c: Symmetric(g2,g8,g-1)
    c: DistanceY(g2,g14) = 234
    c: DistanceX(g2,g5) = 234
    c: DistanceX(g1,g6) = 190
    c: DistanceY(g0,g12) = 200
FEATURE [Sketcher::SketchObject] Sketch036
  FullyConstrained = true
  MapMode = 5
  Support = -> [XY_Plane010]
  expr: Constraints[13] = <<Variables>>.GantorySpacing + (<<Variables>>.CavitySpacingY + <<Variables>>.WallThickness) * 2
  expr: Constraints[14] = <<Variables>>.GantorySpacing + (<<Variables>>.CavitySpacingX + <<Variables>>.WallThickness) * 2
  sketch-geometry (8):
    g0: LineSegment StartX=-112 StartY=117 StartZ=0 EndX=112 EndY=117 EndZ=0
    g1: LineSegment StartX=117 StartY=112 StartZ=0 EndX=117 EndY=-112 EndZ=0
    g2: LineSegment StartX=112 StartY=-117 StartZ=0 EndX=-112 EndY=-117 EndZ=0
    g3: LineSegment StartX=-117 StartY=-112 StartZ=0 EndX=-117 EndY=112 EndZ=0
    g4: LineSegment StartX=-117 StartY=112 StartZ=0 EndX=-112 EndY=117 EndZ=0
    g5: LineSegment StartX=112 StartY=117 StartZ=0 EndX=117 EndY=112 EndZ=0
    g6: LineSegment StartX=-117 StartY=-112 StartZ=0 EndX=-112 EndY=-117 EndZ=0
    g7: LineSegment StartX=117 StartY=-112 StartZ=0 EndX=112 EndY=-117 EndZ=0
  constraints (18):
    c: Coincident(g4,g0)
    c: Coincident(g4,g3)
    c: Coincident(g5,g1)
    c: Coincident(g2,g7)
    c: Coincident(g7,g1)
    c: Coincident(g6,g3)
    c: Coincident(g6,g2)
    c: Symmetric(g3,g3,g-1)
    c: Symmetric(g2,g0,g-1)
    c: Symmetric(g2,g2,g-2)
    c: Symmetric(g3,g1,g-2)
    c: Symmetric(g2,g5,g-1)
    c: Symmetric(g3,g1,g-1)
    c: DistanceY(g2,g0) = 234
    c: DistanceX(g3,g1) = 234
    c: Angle(g6) = -0.785398
    c: DistanceX(g3,g2) = 5
    c: Coincident(g0,g5)
FEATURE [PartDesign::Pad] Pad011  label="Pad TopPanel Base"
  Direction = (0,0,1)
  Length = 100
  Length2 = 10
  Profile = -> Sketch036
  ReferenceAxis = -> Sketch036 [N_Axis]
  Type = 0
FEATURE [PartDesign::SubShapeBinder] Binder007  label="Binder for TopPanel Y Rail Hole Support"
  BindCopyOnChange = 0
  BindMode = 0
  ClaimChildren = false
  Context = -> Part004 [Body004.Binder007.]
  Fuse = false
  MakeFace = true
  OffsetFill = false
  OffsetIntersection = false
  OffsetJoinType = 0
  OffsetOpenResult = false
  PartialLoad = false
  Placement = pos=(0,0,3) rot=(0,0,1;0rad)
  Relative = true
  Support = -> [Hole006[Sketch014.]]
  _Version = 2
FEATURE [PartDesign::SubShapeBinder] Binder008  label="Binder for TopPanel BottomFaceFitting Support"
  BindCopyOnChange = 0
  BindMode = 0
  ClaimChildren = false
  Context = -> Part004 [Body004.Binder008.]
  Fuse = false
  MakeFace = true
  OffsetFill = false
  OffsetIntersection = false
  OffsetJoinType = 0
  OffsetOpenResult = false
  PartialLoad = false
  Placement = pos=(0,0,9) rot=(0,0,1;0rad)
  Relative = true
  Support = -> [Hole009[Sketch032.]]
  _Version = 2
FEATURE [PartDesign::Pocket] Pocket042  label="Pocket TopPanel BaseHeight"
  BaseFeature = -> Pad011
  Direction = (0,1,2e-16)
  Length = 220
  Length2 = 5
  Midplane = true
  Profile = -> Sketch110
  ReferenceAxis = -> Sketch110 [N_Axis]
  Type = 0
  expr: Length = <<Variables>>.GantorySpacing + <<Variables>>.CavitySpacingY * 2
FEATURE [PartDesign::Pocket] Pocket044  label="Pocket TopPanel CutFront"
  BaseFeature = -> Pocket042
  Direction = (0,1,2e-16)
  Length = 5
  Length2 = 5
  Profile = -> Sketch110
  ReferenceAxis = -> Sketch110 [N_Axis]
  Reversed = true
  Type = 1
FEATURE [PartDesign::Pocket] Pocket005  label="Pocket TopPanel BottomFace Left"
  BaseFeature = -> Pocket044
  Direction = (-1,2e-16,-3e-16)
  Length = 7
  Length2 = 5
  Profile = -> Sketch025
  ReferenceAxis = -> Sketch025 [N_Axis]
  Type = 0
  expr: Length = <<Variables>>.WallThickness
FEATURE [PartDesign::Mirrored] Mirrored  label="Mirrored TopPanel BottomFace Right"
  BaseFeature = -> Pocket005
  MirrorPlane = -> YZ_Plane010
  Originals = -> [Pocket005]
FEATURE [PartDesign::Hole] Hole031  label="Hole TopPanel BottomFace LR"
  BaseFeature = -> Mirrored
  CustomThreadClearance = 0
  Depth = 676.187
  DepthType = 1
  Diameter = 2.5
  DrillForDepth = false
  DrillPoint = 1
  DrillPointAngle = 118
  HoleCutCountersinkAngle = 90
  HoleCutCustomValues = false
  HoleCutDepth = 0
  HoleCutDiameter = 6.1
  HoleCutType = 0
  ModelThread = false
  Profile = -> Sketch025
  Tapered = false
  TaperedAngle = 90
  ThreadClass = 0
  ThreadDepth = 676.187
  ThreadDepthType = 0
  ThreadDirection = 0
  ThreadFit = 0
  ThreadSize = 9
  ThreadType = 1
  Threaded = true
  UseCustomThreadClearance = false
FEATURE [PartDesign::Pocket] Pocket010  label="Pocket TopPanel RearFitting"
  BaseFeature = -> Hole031
  Direction = (0,1,2e-16)
  Length = 7
  Length2 = 5
  Profile = -> Sketch031
  ReferenceAxis = -> Sketch031 [N_Axis]
  Reversed = true
  Type = 0
  expr: Length = <<Variables>>.WallThickness
FEATURE [PartDesign::Hole] Hole011  label="Hole TopPanel RearFitting"
  BaseFeature = -> Pocket010
  CustomThreadClearance = 0
  Depth = 25
  DepthType = 0
  Diameter = 2.5
  DrillForDepth = false
  DrillPoint = 1
  DrillPointAngle = 118
  HoleCutCountersinkAngle = 90
  HoleCutCustomValues = false
  HoleCutDepth = 3.4
  HoleCutDiameter = 6.1
  HoleCutType = 0
  ModelThread = false
  Profile = -> Sketch031
  Reversed = true
  Tapered = false
  TaperedAngle = 90
  ThreadClass = 0
  ThreadDepth = 25
  ThreadDepthType = 0
  ThreadDirection = 0
  ThreadFit = 0
  ThreadSize = 9
  ThreadType = 1
  Threaded = true
  UseCustomThreadClearance = false
FEATURE [PartDesign::Pocket] Pocket003  label="Pocket TopPanel Cavity 1"
  BaseFeature = -> Hole011
  Direction = (0,1,2e-16)
  Length = 180
  Length2 = 5
  Midplane = true
  Profile = -> Sketch022
  ReferenceAxis = -> Sketch022 [N_Axis]
  Type = 0
  expr: Length = <<Variables>>.GantorySpacing - 20
FEATURE [PartDesign::Pocket] Pocket004  label="Pocket TopPanel Cavity 2"
  BaseFeature = -> Pocket003
  Direction = (-1,2e-16,-3e-16)
  Length = 220
  Length2 = 5
  Midplane = true
  Profile = -> Sketch023
  ReferenceAxis = -> Sketch023 [N_Axis]
  Type = 0
  expr: Length = <<Variables>>.GantorySpacing + <<Variables>>.CavitySpacingX * 2
FEATURE [PartDesign::Hole] Hole009  label="Hole TopPanel BottomFaceFitting"
  BaseFeature = -> Pocket004
  CustomThreadClearance = 0
  Depth = 25
  DepthType = 0
  Diameter = 3.4
  DrillForDepth = false
  DrillPoint = 1
  DrillPointAngle = 118
  HoleCutCountersinkAngle = 90
  HoleCutCustomValues = false
  HoleCutDepth = 9
  HoleCutDiameter = 6
  HoleCutType = 1
  ModelThread = false
  Profile = -> Sketch032
  Reversed = true
  Tapered = false
  TaperedAngle = 90
  ThreadClass = 0
  ThreadDepth = 25
  ThreadDepthType = 0
  ThreadDirection = 0
  ThreadFit = 0
  ThreadSize = 9
  ThreadType = 1
  Threaded = false
  UseCustomThreadClearance = false
FEATURE [PartDesign::Pad] Pad030  label="Pad TopPanel BottomFaceFitting Support"
  BaseFeature = -> Hole009
  Direction = (0,0,1)
  Length = 0.2
  Length2 = 10
  Profile = -> Binder008
  Reversed = true
  Type = 0
FEATURE [PartDesign::Pad] Pad009  label="Pad TopPanel PullyMount"
  BaseFeature = -> Pad030
  Direction = (0,0,1)
  Length = 60
  Length2 = 10
  Profile = -> Sketch028
  ReferenceAxis = -> Sketch028 [N_Axis]
  Type = 0
  expr: Length = 60
FEATURE [PartDesign::Pad] Pad044  label="Pad TopPanel LimitSwitchMount"
  BaseFeature = -> Pad009
  Direction = (0,0,1)
  Length = 17
  Length2 = 10
  Profile = -> Sketch042
  ReferenceAxis = -> Sketch042 [N_Axis]
  Type = 0
  expr: Length = <<Variables>>.TopThickness + 7
FEATURE [PartDesign::Pocket] Pocket009  label="Pocket TopPanel MotorCut"
  BaseFeature = -> Pad044
  Direction = (0,0,-1)
  Length = 32
  Length2 = 5
  Profile = -> Sketch030
  ReferenceAxis = -> Sketch030 [N_Axis]
  Type = 0
  expr: Length = 60 - <<Variables>>.TopThickness - 17 - 1
FEATURE [PartDesign::Pocket] Pocket011  label="Pocket TopPanel PullyMountFitting"
  BaseFeature = -> Pocket009
  Direction = (0,0,-1)
  Length = 14
  Length2 = 5
  Profile = -> Sketch033
  ReferenceAxis = -> Sketch033 [N_Axis]
  Type = 0
  expr: Length = 60 - <<Variables>>.TopThickness - 17 - 19
FEATURE [PartDesign::Pocket] Pocket012  label="Pocket TopPanel PullyFitting"
  BaseFeature = -> Pocket011
  Direction = (0,0,-1)
  Length = 33
  Length2 = 5
  Profile = -> Sketch037
  ReferenceAxis = -> Sketch037 [N_Axis]
  Type = 0
  expr: Length = 60 - <<Variables>>.TopThickness - 17
FEATURE [PartDesign::Hole] Hole007  label="Hole TopPanel PullyFitting"
  BaseFeature = -> Pocket012
  CustomThreadClearance = 0
  Depth = 688.477
  DepthType = 1
  Diameter = 3.4
  DrillForDepth = false
  DrillPoint = 1
  DrillPointAngle = 118
  HoleCutCountersinkAngle = 90
  HoleCutCustomValues = false
  HoleCutDepth = 21
  HoleCutDiameter = 6
  HoleCutType = 1
  ModelThread = false
  Profile = -> Binder002
  Reversed = true
  Tapered = false
  TaperedAngle = 90
  ThreadClass = 0
  ThreadDepth = 688.477
  ThreadDepthType = 0
  ThreadDirection = 0
  ThreadFit = 0
  ThreadSize = 9
  ThreadType = 1
  Threaded = false
  UseCustomThreadClearance = false
FEATURE [PartDesign::Pad] Pad031  label="Pad TopPanel PullyFitting Support"
  BaseFeature = -> Hole007
  Direction = (0,0,1)
  Length = 0.2
  Length2 = 10
  Profile = -> Sketch088
  ReferenceAxis = -> Sketch088 [N_Axis]
  Type = 0
FEATURE [PartDesign::Hole] Hole041  label="Hole TopPanel FrontLock"
  BaseFeature = -> Pad031
  CustomThreadClearance = 0
  Depth = 25
  DepthType = 0
  Diameter = 2.5
  DrillForDepth = false
  DrillPoint = 1
  DrillPointAngle = 118
  HoleCutCountersinkAngle = 90
  HoleCutCustomValues = false
  HoleCutDepth = 0
  HoleCutDiameter = 6.1
  HoleCutType = 0
  ModelThread = false
  Profile = -> Sketch124
  Tapered = false
  TaperedAngle = 90
  ThreadClass = 0
  ThreadDepth = 25
  ThreadDepthType = 0
  ThreadDirection = 0
  ThreadFit = 0
  ThreadSize = 9
  ThreadType = 1
  Threaded = true
  UseCustomThreadClearance = false
FEATURE [PartDesign::Hole] Hole040  label="Hole TopPanel LimitSwitchMount"
  BaseFeature = -> Hole041
  CustomThreadClearance = 0
  Depth = 25
  DepthType = 0
  Diameter = 1.6
  DrillForDepth = false
  DrillPoint = 1
  DrillPointAngle = 118
  HoleCutCountersinkAngle = 90
  HoleCutCustomValues = false
  HoleCutDepth = 8
  HoleCutDiameter = 4
  HoleCutType = 1
  ModelThread = false
  Profile = -> Sketch042
  Reversed = true
  Tapered = false
  TaperedAngle = 90
  ThreadClass = 0
  ThreadDepth = 25
  ThreadDepthType = 0
  ThreadDirection = 0
  ThreadFit = 0
  ThreadSize = 6
  ThreadType = 1
  Threaded = true
  UseCustomThreadClearance = false
  expr: HoleCutDepth = <<Variables>>.TopThickness + 7 - 9
FEATURE [PartDesign::Pad] Pad045  label="Pad TopPanel LimitSwitchMount Support"
  BaseFeature = -> Hole040
  Direction = (0,0,1)
  Length = 0.2
  Length2 = 10
  Profile = -> Sketch111
  ReferenceAxis = -> Sketch111 [N_Axis]
  Type = 0
FEATURE [PartDesign::Pocket] Pocket028  label="Pocket TopPanel TopWindow"
  BaseFeature = -> Pad045
  Direction = (0,0,-1)
  Length = 20
  Length2 = 5
  Midplane = true
  Profile = -> Sketch038
  ReferenceAxis = -> Sketch038 [N_Axis]
  Type = 0
  expr: Length = <<Variables>>.TopThickness * 2
FEATURE [PartDesign::SubtractiveLoft] SubtractiveLoft001  label="SubtractiveLoft TopPanel TopWindow 1"
  BaseFeature = -> Pocket028
  Closed = false
  Profile = -> Sketch038
  Ruled = false
  Sections = -> [Sketch084]
FEATURE [PartDesign::SubtractiveLoft] SubtractiveLoft002  label="SubtractiveLoft TopPanel TopWindow 2"
  BaseFeature = -> SubtractiveLoft001
  Closed = false
  Profile = -> Sketch085
  Ruled = false
  Sections = -> [Sketch086]
FEATURE [PartDesign::Pocket] Pocket029  label="Pocket TopPanel FrontWindow"
  BaseFeature = -> SubtractiveLoft002
  Direction = (0,1,2e-16)
  Length = 14
  Length2 = 5
  Midplane = true
  Profile = -> Sketch082
  ReferenceAxis = -> Sketch082 [N_Axis]
  Type = 0
  expr: Length = <<Variables>>.WallThickness * 2
FEATURE [PartDesign::SubtractiveLoft] SubtractiveLoft  label="SubtractiveLoft TopPanel FrontWindow"
  BaseFeature = -> Pocket029
  Closed = false
  Profile = -> Sketch082
  Ruled = false
  Sections = -> [Sketch083]
FEATURE [PartDesign::Hole] Hole006  label="Hole TopPanel Y Rail"
  BaseFeature = -> SubtractiveLoft
  CustomThreadClearance = 0
  Depth = 10
  DepthType = 0
  Diameter = 2.5
  DrillForDepth = false
  DrillPoint = 1
  DrillPointAngle = 118
  HoleCutCountersinkAngle = 90
  HoleCutCustomValues = false
  HoleCutDepth = 3.4
  HoleCutDiameter = 6
  HoleCutType = 0
  ModelThread = false
  Profile = -> Sketch014
  Tapered = false
  TaperedAngle = 90
  ThreadClass = 0
  ThreadDepth = 10
  ThreadDepthType = 0
  ThreadDirection = 0
  ThreadFit = 0
  ThreadSize = 9
  ThreadType = 1
  Threaded = true
  UseCustomThreadClearance = false
  expr: Depth = <<Variables>>.TopThickness
FEATURE [PartDesign::Pad] Pad029  label="Pad TopPanel Y Rail Hole Support"
  BaseFeature = -> Hole006
  Direction = (0,0,1)
  Length = 0.2
  Length2 = 10
  Profile = -> Binder007
  Type = 0
FEATURE [PartDesign::Hole] Hole014  label="Hole TopPanel RearCap"
  BaseFeature = -> Pad029
  CustomThreadClearance = 0
  Depth = 681.607
  DepthType = 1
  Diameter = 2.5
  DrillForDepth = false
  DrillPoint = 1
  DrillPointAngle = 118
  HoleCutCountersinkAngle = 90
  HoleCutCustomValues = false
  HoleCutDepth = 0
  HoleCutDiameter = 6.1
  HoleCutType = 0
  ModelThread = false
  Profile = -> Sketch041
  Reversed = true
  Tapered = false
  TaperedAngle = 90
  ThreadClass = 0
  ThreadDepth = 681.607
  ThreadDepthType = 0
  ThreadDirection = 0
  ThreadFit = 0
  ThreadSize = 9
  ThreadType = 1
  Threaded = true
  UseCustomThreadClearance = false
FEATURE [PartDesign::Body] Body004  label="TopPanelPlate"
  Group = -> [Local_CS,Sketch036,Pad011,Pocket042,Pocket044,Pocket005,Mirrored,Hole031,Pocket010,Hole011,Pocket003,Pocket004,Hole009,Binder008,Pad030,Sketch028,Pad009,Pad044,Sketch030,Pocket009,Sketch031,Sketch032,Sketch033,Pocket011,Pocket012,Hole007,Pad031,Hole041,Hole040,Pad045,Pocket028,SubtractiveLoft001,SubtractiveLoft002,Pocket029,SubtractiveLoft,Hole006,Binder007,Pad029,Hole014,Sketch014,Sketch022,+26 more]
  Origin = -> Origin010
  Tip = -> Boolean004
